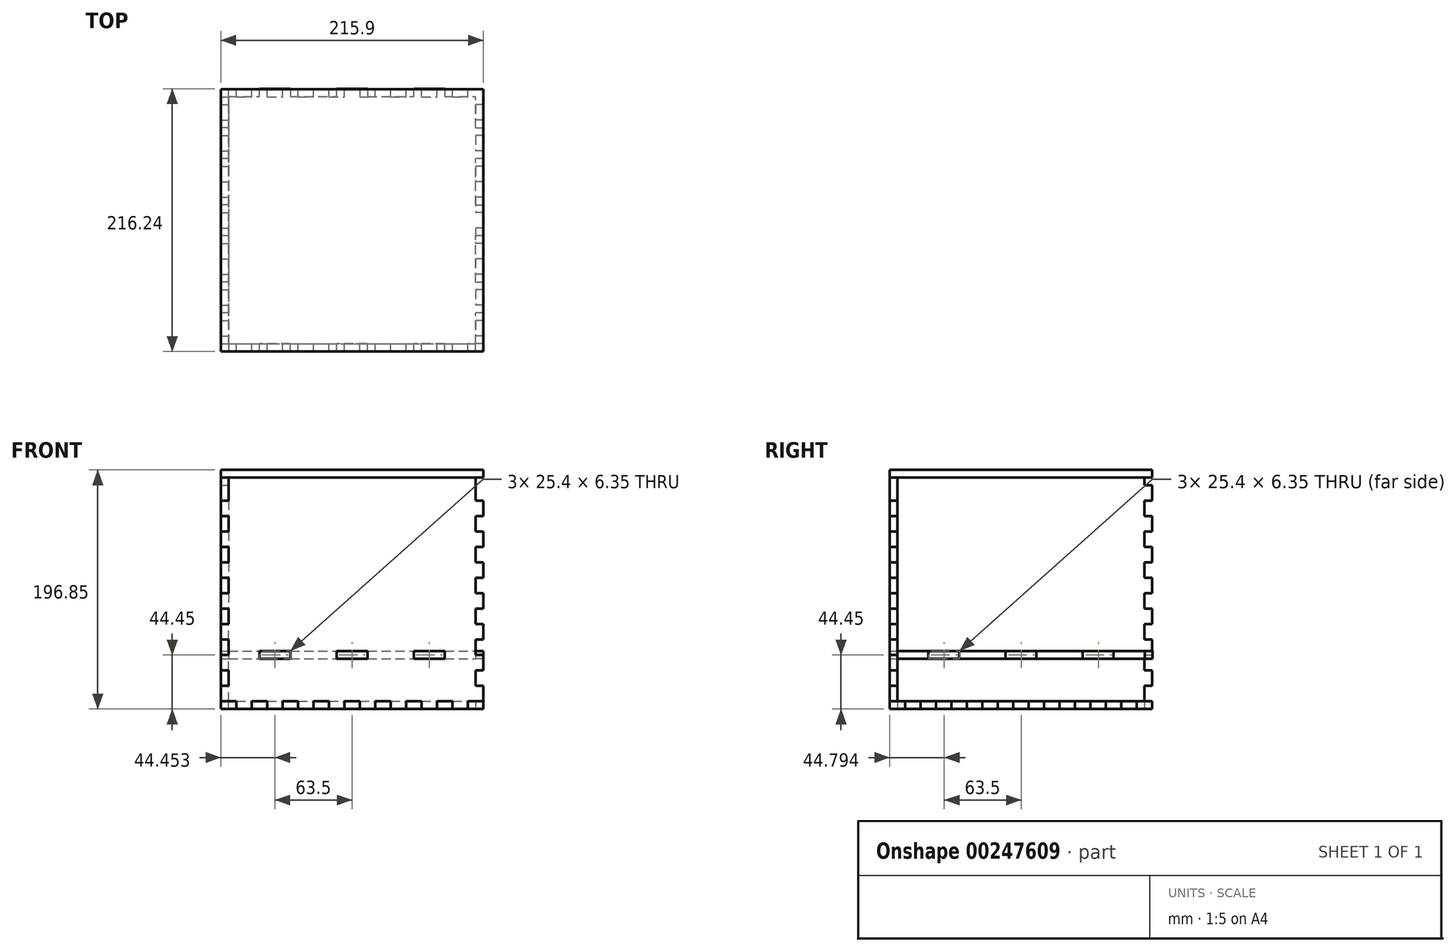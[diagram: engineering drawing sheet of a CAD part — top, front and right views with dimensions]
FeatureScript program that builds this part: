
annotation { "Feature Type Name" : "Feature", "Feature Type Description" : "" }
export const myFeature = defineFeature(function(context is Context, id is Id, definition is map)
    precondition{}
    {
        {
            var Q0;
            Q0=qCreatedBy(makeId("Top.planeOp"),FACE);
            var sketch = newSketch(context, id + "F0", { "sketchPlane" : qUnion([Q0])});
            skLineSegment(sketch, "E0.bottom", {"start": v(-61.86, 103.32) * mm, "end": v(-49.16, 103.32) * mm});
            skLineSegment(sketch, "E0.top", {"start": v(-61.86, -99.88) * mm, "end": v(-49.16, -99.88) * mm});
            skLineSegment(sketch, "E0.left", {"start": v(-68.2, 96.97) * mm, "end": v(-68.2, 84.27) * mm});
            skLineSegment(sketch, "E1.top", {"start": v(33.4, 109.67) * mm, "end": v(27.04, 109.67) * mm});
            skLineSegment(sketch, "E1.right", {"start": v(27.04, 103.32) * mm, "end": v(27.04, 109.67) * mm});
            skLineSegment(sketch, "E2.bottom", {"start": v(33.4, 109.67) * mm, "end": v(39.74, 109.67) * mm});
            skLineSegment(sketch, "E2.right", {"start": v(39.74, 109.67) * mm, "end": v(39.74, 103.32) * mm});
            skLineSegment(sketch, "E3.1.0.0", {"start": v(14.34, 103.32) * mm, "end": v(14.34, 109.67) * mm});
            skLineSegment(sketch, "E3.2.0.0", {"start": v(1.64, 103.32) * mm, "end": v(1.64, 109.67) * mm});
            skLineSegment(sketch, "E3.3.0.0", {"start": v(-11.06, 103.32) * mm, "end": v(-11.06, 109.67) * mm});
            skLineSegment(sketch, "E3.4.0.0", {"start": v(-23.76, 103.32) * mm, "end": v(-23.76, 109.67) * mm});
            skLineSegment(sketch, "E3.5.0.0", {"start": v(-36.46, 103.32) * mm, "end": v(-36.46, 109.67) * mm});
            skLineSegment(sketch, "E3.6.0.0", {"start": v(-49.16, 103.32) * mm, "end": v(-49.16, 109.67) * mm});
            skLineSegment(sketch, "E3.7.0.0", {"start": v(-61.86, 103.32) * mm, "end": v(-61.86, 109.67) * mm});
            skLineSegment(sketch, "E3.direction1", {"start": v(27.04, 103.32) * mm, "end": v(14.34, 103.32) * mm, "construction": true});
            skLineSegment(sketch, "E4", {"start": v(14.34, 109.67) * mm, "end": v(1.64, 109.67) * mm});
            skLineSegment(sketch, "E5", {"start": v(-23.76, 109.67) * mm, "end": v(-11.06, 109.67) * mm});
            skLineSegment(sketch, "E6", {"start": v(-36.46, 109.67) * mm, "end": v(-49.16, 109.67) * mm});
            skLineSegment(sketch, "E7", {"start": v(-68.2, 109.67) * mm, "end": v(-61.86, 109.67) * mm});
            skLineSegment(sketch, "E8.trimOffspring", {"start": v(-36.46, 103.32) * mm, "end": v(-23.76, 103.32) * mm});
            skLineSegment(sketch, "E9.trimOffspring", {"start": v(-11.06, 103.32) * mm, "end": v(1.64, 103.32) * mm});
            skLineSegment(sketch, "E10.trimOffspring", {"start": v(14.34, 103.32) * mm, "end": v(27.04, 103.32) * mm});
            skPoint(sketch, "E1.bottom.start.orphan", {"position": v(33.4, 103.32) * mm});
            skLineSegment(sketch, "E11.MirrorCS", {"start": v(135, 109.67) * mm, "end": v(128.64, 109.67) * mm});
            skLineSegment(sketch, "E12.MirrorCS", {"start": v(128.64, 103.32) * mm, "end": v(128.64, 109.67) * mm});
            skLineSegment(sketch, "E13.MirrorCS", {"start": v(103.24, 109.67) * mm, "end": v(115.94, 109.67) * mm});
            skLineSegment(sketch, "E14.MirrorCS", {"start": v(115.94, 103.32) * mm, "end": v(115.94, 109.67) * mm});
            skLineSegment(sketch, "E15.MirrorCS", {"start": v(103.24, 103.32) * mm, "end": v(103.24, 109.67) * mm});
            skLineSegment(sketch, "E16.MirrorCS", {"start": v(90.54, 103.32) * mm, "end": v(90.54, 109.67) * mm});
            skLineSegment(sketch, "E17.MirrorCS", {"start": v(90.54, 109.67) * mm, "end": v(77.84, 109.67) * mm});
            skLineSegment(sketch, "E18.MirrorCS", {"start": v(77.84, 103.32) * mm, "end": v(77.84, 109.67) * mm});
            skLineSegment(sketch, "E19.MirrorCS", {"start": v(65.14, 103.32) * mm, "end": v(65.14, 109.67) * mm});
            skLineSegment(sketch, "E20.MirrorCS", {"start": v(52.44, 109.67) * mm, "end": v(65.14, 109.67) * mm});
            skLineSegment(sketch, "E21.MirrorCS", {"start": v(52.44, 103.32) * mm, "end": v(52.44, 109.67) * mm});
            skLineSegment(sketch, "E22", {"start": v(39.74, 103.32) * mm, "end": v(52.44, 103.32) * mm});
            skLineSegment(sketch, "E23", {"start": v(65.14, 103.32) * mm, "end": v(77.84, 103.32) * mm});
            skLineSegment(sketch, "E24", {"start": v(90.54, 103.32) * mm, "end": v(103.24, 103.32) * mm});
            skLineSegment(sketch, "E25", {"start": v(115.94, 103.32) * mm, "end": v(128.64, 103.32) * mm});
            skLineSegment(sketch, "E26.MirrorCS", {"start": v(103.24, -106.23) * mm, "end": v(115.94, -106.23) * mm});
            skLineSegment(sketch, "E27.MirrorCS", {"start": v(27.04, -99.88) * mm, "end": v(27.04, -106.23) * mm});
            skLineSegment(sketch, "E28.MirrorCS", {"start": v(128.64, -99.88) * mm, "end": v(128.64, -106.23) * mm});
            skLineSegment(sketch, "E29.MirrorCS", {"start": v(33.4, -106.23) * mm, "end": v(39.74, -106.23) * mm});
            skLineSegment(sketch, "E30.MirrorCS", {"start": v(-49.16, -99.88) * mm, "end": v(-49.16, -106.23) * mm});
            skLineSegment(sketch, "E31.MirrorCS", {"start": v(-11.06, -99.88) * mm, "end": v(-11.06, -106.23) * mm});
            skLineSegment(sketch, "E32.MirrorCS", {"start": v(-61.86, -99.88) * mm, "end": v(-61.86, -106.23) * mm});
            skLineSegment(sketch, "E33.MirrorCS", {"start": v(39.74, -106.23) * mm, "end": v(39.74, -99.88) * mm});
            skLineSegment(sketch, "E34.MirrorCS", {"start": v(-68.2, -106.23) * mm, "end": v(-61.86, -106.23) * mm});
            skLineSegment(sketch, "E35.MirrorCS", {"start": v(90.54, -106.23) * mm, "end": v(77.84, -106.23) * mm});
            skLineSegment(sketch, "E36.MirrorCS", {"start": v(14.34, -106.23) * mm, "end": v(1.64, -106.23) * mm});
            skLineSegment(sketch, "E37.MirrorCS", {"start": v(-36.46, -99.88) * mm, "end": v(-36.46, -106.23) * mm});
            skLineSegment(sketch, "E38.MirrorCS", {"start": v(52.44, -99.88) * mm, "end": v(52.44, -106.23) * mm});
            skLineSegment(sketch, "E39.MirrorCS", {"start": v(135, -106.23) * mm, "end": v(128.64, -106.23) * mm});
            skLineSegment(sketch, "E40.MirrorCS", {"start": v(33.4, -106.23) * mm, "end": v(27.04, -106.23) * mm});
            skLineSegment(sketch, "E41.MirrorCS", {"start": v(77.84, -99.88) * mm, "end": v(77.84, -106.23) * mm});
            skLineSegment(sketch, "E42.MirrorCS", {"start": v(-36.46, -106.23) * mm, "end": v(-49.16, -106.23) * mm});
            skLineSegment(sketch, "E43.MirrorCS", {"start": v(103.24, -99.88) * mm, "end": v(103.24, -106.23) * mm});
            skLineSegment(sketch, "E44.MirrorCS", {"start": v(52.44, -106.23) * mm, "end": v(65.14, -106.23) * mm});
            skLineSegment(sketch, "E45.MirrorCS", {"start": v(-23.76, -106.23) * mm, "end": v(-11.06, -106.23) * mm});
            skLineSegment(sketch, "E46.MirrorCS", {"start": v(65.14, -99.88) * mm, "end": v(65.14, -106.23) * mm});
            skPoint(sketch, "E47.MirrorP", {"position": v(33.4, -99.88) * mm});
            skLineSegment(sketch, "E48.MirrorCS", {"start": v(14.34, -99.88) * mm, "end": v(14.34, -106.23) * mm});
            skLineSegment(sketch, "E49.MirrorCS", {"start": v(115.94, -99.88) * mm, "end": v(115.94, -106.23) * mm});
            skLineSegment(sketch, "E50.MirrorCS", {"start": v(90.54, -99.88) * mm, "end": v(90.54, -106.23) * mm});
            skLineSegment(sketch, "E51.MirrorCS", {"start": v(1.64, -99.88) * mm, "end": v(1.64, -106.23) * mm});
            skLineSegment(sketch, "E52.MirrorCS", {"start": v(-23.76, -99.88) * mm, "end": v(-23.76, -106.23) * mm});
            skLineSegment(sketch, "E53.trimOffspring", {"start": v(-36.46, -99.88) * mm, "end": v(-23.76, -99.88) * mm});
            skLineSegment(sketch, "E54.trimOffspring", {"start": v(-11.06, -99.88) * mm, "end": v(1.64, -99.88) * mm});
            skLineSegment(sketch, "E55.trimOffspring", {"start": v(14.34, -99.88) * mm, "end": v(27.04, -99.88) * mm});
            skLineSegment(sketch, "E56.trimOffspring", {"start": v(39.74, -99.88) * mm, "end": v(52.44, -99.88) * mm});
            skLineSegment(sketch, "E57.trimOffspring", {"start": v(65.14, -99.88) * mm, "end": v(77.84, -99.88) * mm});
            skLineSegment(sketch, "E58.trimOffspring", {"start": v(90.54, -99.88) * mm, "end": v(103.24, -99.88) * mm});
            skLineSegment(sketch, "E59.trimOffspring", {"start": v(115.94, -99.88) * mm, "end": v(128.64, -99.88) * mm});
            skPoint(sketch, "E60.start.orphan", {"position": v(-68.2, 1.72) * mm});
            skLineSegment(sketch, "E61.bottom", {"start": v(-74.56, 8.07) * mm, "end": v(-68.2, 8.07) * mm});
            skLineSegment(sketch, "E61.top", {"start": v(-74.56, -4.63) * mm, "end": v(-68.2, -4.63) * mm});
            skLineSegment(sketch, "E61.left", {"start": v(-74.56, 8.07) * mm, "end": v(-74.56, -4.63) * mm});
            skPoint(sketch, "E61.right.start.orphan", {"position": v(-61.86, 8.07) * mm});
            skPoint(sketch, "E62.orphan", {"position": v(-61.86, -4.63) * mm});
            skLineSegment(sketch, "E63.1.0.0", {"start": v(-74.56, 20.77) * mm, "end": v(-68.2, 20.77) * mm});
            skLineSegment(sketch, "E63.2.0.0", {"start": v(-74.56, 33.47) * mm, "end": v(-68.2, 33.47) * mm});
            skLineSegment(sketch, "E63.3.0.0", {"start": v(-74.56, 46.17) * mm, "end": v(-68.2, 46.17) * mm});
            skLineSegment(sketch, "E63.4.0.0", {"start": v(-74.56, 58.87) * mm, "end": v(-68.2, 58.87) * mm});
            skLineSegment(sketch, "E64", {"start": v(-74.56, 20.77) * mm, "end": v(-74.56, 33.47) * mm});
            skLineSegment(sketch, "E65", {"start": v(-74.56, 46.17) * mm, "end": v(-74.56, 58.87) * mm});
            skLineSegment(sketch, "E66.1.0.0", {"start": v(-74.56, -17.33) * mm, "end": v(-68.2, -17.33) * mm});
            skLineSegment(sketch, "E66.2.0.0", {"start": v(-74.56, -30.03) * mm, "end": v(-68.2, -30.03) * mm});
            skLineSegment(sketch, "E66.3.0.0", {"start": v(-74.56, -42.73) * mm, "end": v(-68.2, -42.73) * mm});
            skLineSegment(sketch, "E66.4.0.0", {"start": v(-74.56, -55.43) * mm, "end": v(-68.2, -55.43) * mm});
            skLineSegment(sketch, "E67", {"start": v(-74.56, -17.33) * mm, "end": v(-74.56, -30.03) * mm});
            skLineSegment(sketch, "E68", {"start": v(-74.56, -42.73) * mm, "end": v(-74.56, -55.43) * mm});
            skLineSegment(sketch, "E69.trimOffspring", {"start": v(-68.2, -55.43) * mm, "end": v(-68.2, -68.13) * mm});
            skLineSegment(sketch, "E70.trimOffspring", {"start": v(-68.2, -30.03) * mm, "end": v(-68.2, -42.73) * mm});
            skLineSegment(sketch, "E71.trimOffspring", {"start": v(-68.2, 20.77) * mm, "end": v(-68.2, 8.07) * mm});
            skLineSegment(sketch, "E72.trimOffspring", {"start": v(-68.2, 46.17) * mm, "end": v(-68.2, 33.47) * mm});
            skLineSegment(sketch, "E73.trimOffspring", {"start": v(-68.2, -4.63) * mm, "end": v(-68.2, -17.33) * mm});
            skLineSegment(sketch, "E74.1.0.0", {"start": v(-74.56, 71.57) * mm, "end": v(-68.2, 71.57) * mm});
            skLineSegment(sketch, "E74.2.0.0", {"start": v(-74.56, 84.27) * mm, "end": v(-68.2, 84.27) * mm});
            skLineSegment(sketch, "E75.0.3.0", {"start": v(-74.56, 96.97) * mm, "end": v(-68.2, 96.97) * mm});
            skLineSegment(sketch, "E76", {"start": v(-74.56, 71.57) * mm, "end": v(-74.56, 84.27) * mm});
            skLineSegment(sketch, "E77", {"start": v(-74.56, 96.97) * mm, "end": v(-74.56, 109.67) * mm});
            skLineSegment(sketch, "E78", {"start": v(-74.56, 109.67) * mm, "end": v(-68.2, 109.67) * mm});
            skPoint(sketch, "E79.orphan", {"position": v(-68.2, 103.32) * mm});
            skLineSegment(sketch, "E80.trimOffspring", {"start": v(-68.2, 71.57) * mm, "end": v(-68.2, 58.87) * mm});
            skLineSegment(sketch, "E81", {"start": v(135, 96.97) * mm, "end": v(135, 84.27) * mm});
            skLineSegment(sketch, "E82", {"start": v(33.4, 103.32) * mm, "end": v(33.4, -99.88) * mm});
            skLineSegment(sketch, "E83.MirrorCS", {"start": v(141.34, -55.43) * mm, "end": v(135, -55.43) * mm});
            skLineSegment(sketch, "E84.MirrorCS", {"start": v(141.34, -4.63) * mm, "end": v(135, -4.63) * mm});
            skLineSegment(sketch, "E85.MirrorCS", {"start": v(141.34, 33.47) * mm, "end": v(135, 33.47) * mm});
            skLineSegment(sketch, "E86.MirrorCS", {"start": v(141.34, 20.77) * mm, "end": v(135, 20.77) * mm});
            skLineSegment(sketch, "E87.MirrorCS", {"start": v(141.34, 8.07) * mm, "end": v(135, 8.07) * mm});
            skLineSegment(sketch, "E88.MirrorCS", {"start": v(141.34, 96.97) * mm, "end": v(141.34, 109.67) * mm});
            skLineSegment(sketch, "E89.MirrorCS", {"start": v(141.34, -17.33) * mm, "end": v(135, -17.33) * mm});
            skLineSegment(sketch, "E90.MirrorCS", {"start": v(141.34, -30.03) * mm, "end": v(135, -30.03) * mm});
            skLineSegment(sketch, "E91.MirrorCS", {"start": v(141.34, 71.57) * mm, "end": v(135, 71.57) * mm});
            skLineSegment(sketch, "E92.MirrorCS", {"start": v(141.34, -42.73) * mm, "end": v(135, -42.73) * mm});
            skLineSegment(sketch, "E93.MirrorCS", {"start": v(141.34, 58.87) * mm, "end": v(135, 58.87) * mm});
            skLineSegment(sketch, "E94.MirrorCS", {"start": v(141.34, 46.17) * mm, "end": v(135, 46.17) * mm});
            skLineSegment(sketch, "E95.MirrorCS", {"start": v(141.34, 96.97) * mm, "end": v(135, 96.97) * mm});
            skLineSegment(sketch, "E96.MirrorCS", {"start": v(141.34, 84.27) * mm, "end": v(135, 84.27) * mm});
            skPoint(sketch, "E97.MirrorP", {"position": v(135, 1.72) * mm});
            skLineSegment(sketch, "E98.MirrorCS", {"start": v(141.34, -17.33) * mm, "end": v(141.34, -30.03) * mm});
            skLineSegment(sketch, "E99.MirrorCS", {"start": v(141.34, 46.17) * mm, "end": v(141.34, 58.87) * mm});
            skLineSegment(sketch, "E100.MirrorCS", {"start": v(141.34, 8.07) * mm, "end": v(141.34, -4.63) * mm});
            skLineSegment(sketch, "E101.MirrorCS", {"start": v(141.34, 20.77) * mm, "end": v(141.34, 33.47) * mm});
            skLineSegment(sketch, "E102.MirrorCS", {"start": v(141.34, 71.57) * mm, "end": v(141.34, 84.27) * mm});
            skLineSegment(sketch, "E103.MirrorCS", {"start": v(141.34, -42.73) * mm, "end": v(141.34, -55.43) * mm});
            skPoint(sketch, "E104.MirrorP", {"position": v(135, 103.32) * mm});
            skLineSegment(sketch, "E105", {"start": v(135, 109.67) * mm, "end": v(141.34, 109.67) * mm});
            skLineSegment(sketch, "E106.trimOffspring", {"start": v(135, 71.57) * mm, "end": v(135, 58.87) * mm});
            skLineSegment(sketch, "E107.trimOffspring", {"start": v(135, 46.17) * mm, "end": v(135, 33.47) * mm});
            skLineSegment(sketch, "E108.trimOffspring", {"start": v(135, 20.77) * mm, "end": v(135, 8.07) * mm});
            skLineSegment(sketch, "E109.trimOffspring", {"start": v(135, -4.63) * mm, "end": v(135, -17.33) * mm});
            skLineSegment(sketch, "E110.trimOffspring", {"start": v(135, -30.03) * mm, "end": v(135, -42.73) * mm});
            skLineSegment(sketch, "E111.trimOffspring", {"start": v(135, -55.43) * mm, "end": v(135, -68.13) * mm});
            skLineSegment(sketch, "E112.1.0.0", {"start": v(-74.56, -68.13) * mm, "end": v(-68.2, -68.13) * mm});
            skLineSegment(sketch, "E112.2.0.0", {"start": v(-74.56, -80.83) * mm, "end": v(-68.2, -80.83) * mm});
            skLineSegment(sketch, "E112.3.0.0", {"start": v(-74.56, -93.53) * mm, "end": v(-68.2, -93.53) * mm});
            skLineSegment(sketch, "E113", {"start": v(-74.56, -68.13) * mm, "end": v(-74.56, -80.83) * mm});
            skLineSegment(sketch, "E114", {"start": v(-74.56, -93.53) * mm, "end": v(-74.56, -106.23) * mm});
            skLineSegment(sketch, "E115", {"start": v(-74.56, -106.23) * mm, "end": v(-68.2, -106.23) * mm});
            skLineSegment(sketch, "E116.trimOffspring", {"start": v(-68.2, -80.83) * mm, "end": v(-68.2, -93.53) * mm});
            skPoint(sketch, "E117.orphan", {"position": v(-68.2, -99.88) * mm});
            skLineSegment(sketch, "E118.MirrorCS", {"start": v(141.34, -93.53) * mm, "end": v(141.34, -106.23) * mm});
            skLineSegment(sketch, "E119.MirrorCS", {"start": v(141.34, -80.83) * mm, "end": v(135, -80.83) * mm});
            skLineSegment(sketch, "E120.MirrorCS", {"start": v(141.34, -68.13) * mm, "end": v(135, -68.13) * mm});
            skLineSegment(sketch, "E121.MirrorCS", {"start": v(141.34, -68.13) * mm, "end": v(141.34, -80.83) * mm});
            skLineSegment(sketch, "E122.MirrorCS", {"start": v(141.34, -93.53) * mm, "end": v(135, -93.53) * mm});
            skLineSegment(sketch, "E123.MirrorCS", {"start": v(141.34, -106.23) * mm, "end": v(135, -106.23) * mm});
            skLineSegment(sketch, "E124.trimOffspring", {"start": v(135, -80.83) * mm, "end": v(135, -93.53) * mm});
            skPoint(sketch, "E125.MirrorCS.end.orphan", {"position": v(135, -106.23) * mm});
            skSolve(sketch);
        }
        {
            var Q0;
            Q0 = qSketchRegion(id + "F0", true);
            extrude(context, id + "F1", {"entities" : qUnion([Q0]), "depth" : 6.35 * mm, "offsetDistance" : 25.4 * mm});
        }
        {
            var Q0;
            Q0=makeQuery(id+"F1.opExtrude","SWEPT_FACE",FACE,{"disambiguationData":[OSD([sQuery(id+"F0.wireOp",EDGE,"E55.trimOffspring")])]});
            var sketch = newSketch(context, id + "F2", { "sketchPlane" : qUnion([Q0])});
            skLineSegment(sketch, "E126.0.0", {"start": v(14.34, 0) * mm, "end": v(27.04, 0) * mm});
            skLineSegment(sketch, "E126.0.1", {"start": v(27.04, 0) * mm, "end": v(27.04, 6.35) * mm});
            skLineSegment(sketch, "E126.0.3", {"start": v(14.34, 6.35) * mm, "end": v(14.34, 0) * mm});
            skLineSegment(sketch, "E127.0.0", {"start": v(-11.06, 0) * mm, "end": v(1.64, 0) * mm});
            skLineSegment(sketch, "E127.0.1", {"start": v(1.64, 0) * mm, "end": v(1.64, 6.35) * mm});
            skLineSegment(sketch, "E127.0.3", {"start": v(-11.06, 6.35) * mm, "end": v(-11.06, 0) * mm});
            skLineSegment(sketch, "E128.0.0", {"start": v(-36.46, 0) * mm, "end": v(-23.76, 0) * mm});
            skLineSegment(sketch, "E128.0.1", {"start": v(-23.76, 0) * mm, "end": v(-23.76, 6.35) * mm});
            skLineSegment(sketch, "E128.0.3", {"start": v(-36.46, 6.35) * mm, "end": v(-36.46, 0) * mm});
            skLineSegment(sketch, "E129.0.0", {"start": v(-61.86, 0) * mm, "end": v(-49.16, 0) * mm});
            skLineSegment(sketch, "E129.0.1", {"start": v(-49.16, 0) * mm, "end": v(-49.16, 6.35) * mm});
            skLineSegment(sketch, "E129.0.3", {"start": v(-61.86, 6.35) * mm, "end": v(-61.86, 0) * mm});
            skPoint(sketch, "E130.0", {"position": v(46.1, 6.35) * mm});
            skLineSegment(sketch, "E131.0.0", {"start": v(39.74, 0) * mm, "end": v(52.44, 0) * mm});
            skLineSegment(sketch, "E131.0.1", {"start": v(52.44, 0) * mm, "end": v(52.44, 6.35) * mm});
            skLineSegment(sketch, "E131.0.3", {"start": v(39.74, 6.35) * mm, "end": v(39.74, 0) * mm});
            skLineSegment(sketch, "E131.1.0", {"start": v(65.14, 0) * mm, "end": v(77.84, 0) * mm});
            skLineSegment(sketch, "E131.1.1", {"start": v(77.84, 0) * mm, "end": v(77.84, 6.35) * mm});
            skLineSegment(sketch, "E131.1.3", {"start": v(65.14, 6.35) * mm, "end": v(65.14, 0) * mm});
            skLineSegment(sketch, "E131.2.0", {"start": v(90.54, 0) * mm, "end": v(103.24, 0) * mm});
            skLineSegment(sketch, "E131.2.1", {"start": v(103.24, 0) * mm, "end": v(103.24, 6.35) * mm});
            skLineSegment(sketch, "E131.2.3", {"start": v(90.54, 6.35) * mm, "end": v(90.54, 0) * mm});
            skLineSegment(sketch, "E131.3.0", {"start": v(115.94, 0) * mm, "end": v(128.64, 0) * mm});
            skLineSegment(sketch, "E131.3.1", {"start": v(128.64, 0) * mm, "end": v(128.64, 6.35) * mm});
            skLineSegment(sketch, "E131.3.3", {"start": v(115.94, 6.35) * mm, "end": v(115.94, 0) * mm});
            skLineSegment(sketch, "E132", {"start": v(-49.16, 6.35) * mm, "end": v(-36.46, 6.35) * mm});
            skLineSegment(sketch, "E133", {"start": v(-23.76, 6.35) * mm, "end": v(-11.06, 6.35) * mm});
            skLineSegment(sketch, "E134", {"start": v(1.64, 6.35) * mm, "end": v(14.34, 6.35) * mm});
            skLineSegment(sketch, "E135", {"start": v(27.04, 6.35) * mm, "end": v(39.74, 6.35) * mm});
            skLineSegment(sketch, "E136", {"start": v(52.44, 6.35) * mm, "end": v(65.14, 6.35) * mm});
            skLineSegment(sketch, "E137", {"start": v(77.84, 6.35) * mm, "end": v(90.54, 6.35) * mm});
            skLineSegment(sketch, "E138", {"start": v(103.24, 6.35) * mm, "end": v(115.94, 6.35) * mm});
            skPoint(sketch, "E139.end.orphan", {"position": v(33.4, 6.35) * mm});
            skLineSegment(sketch, "E140", {"start": v(-68.2, 184.15) * mm, "end": v(-68.2, 171.45) * mm});
            skLineSegment(sketch, "E141.MirrorCS", {"start": v(-74.56, 19.05) * mm, "end": v(-68.2, 19.05) * mm});
            skLineSegment(sketch, "E142.MirrorCS", {"start": v(-74.56, 31.75) * mm, "end": v(-68.2, 31.75) * mm});
            skLineSegment(sketch, "E143.MirrorCS", {"start": v(-74.56, 107.95) * mm, "end": v(-68.2, 107.95) * mm});
            skLineSegment(sketch, "E144.MirrorCS", {"start": v(-74.56, 57.15) * mm, "end": v(-68.2, 57.15) * mm});
            skLineSegment(sketch, "E145.MirrorCS", {"start": v(-74.56, 171.45) * mm, "end": v(-68.2, 171.45) * mm});
            skLineSegment(sketch, "E146.MirrorCS", {"start": v(-74.56, 44.45) * mm, "end": v(-68.2, 44.45) * mm});
            skLineSegment(sketch, "E147.MirrorCS", {"start": v(-74.56, 158.75) * mm, "end": v(-68.2, 158.75) * mm});
            skLineSegment(sketch, "E148.MirrorCS", {"start": v(-74.56, 82.55) * mm, "end": v(-68.2, 82.55) * mm});
            skLineSegment(sketch, "E149.MirrorCS", {"start": v(-74.56, 69.85) * mm, "end": v(-68.2, 69.85) * mm});
            skLineSegment(sketch, "E150.MirrorCS", {"start": v(-74.56, 120.65) * mm, "end": v(-68.2, 120.65) * mm});
            skLineSegment(sketch, "E151.MirrorCS", {"start": v(-74.56, 6.35) * mm, "end": v(-68.2, 6.35) * mm});
            skLineSegment(sketch, "E152.MirrorCS", {"start": v(-74.56, 133.35) * mm, "end": v(-68.2, 133.35) * mm});
            skLineSegment(sketch, "E153.MirrorCS", {"start": v(-74.56, 95.25) * mm, "end": v(-68.2, 95.25) * mm});
            skLineSegment(sketch, "E154.MirrorCS", {"start": v(-74.56, 146.05) * mm, "end": v(-68.2, 146.05) * mm});
            skLineSegment(sketch, "E155.MirrorCS", {"start": v(-74.56, 171.45) * mm, "end": v(-74.56, 158.75) * mm});
            skLineSegment(sketch, "E156.MirrorCS", {"start": v(-74.56, 69.85) * mm, "end": v(-74.56, 57.15) * mm});
            skPoint(sketch, "E157.MirrorP", {"position": v(-68.2, 88.9) * mm});
            skLineSegment(sketch, "E158.MirrorCS", {"start": v(-74.56, 95.25) * mm, "end": v(-74.56, 82.55) * mm});
            skLineSegment(sketch, "E159.MirrorCS", {"start": v(-61.86, 6.35) * mm, "end": v(-61.86, 6.35) * mm});
            skLineSegment(sketch, "E160.MirrorCS", {"start": v(-74.56, 6.35) * mm, "end": v(-74.56, 19.05) * mm});
            skLineSegment(sketch, "E161.MirrorCS", {"start": v(-74.56, 31.75) * mm, "end": v(-74.56, 44.45) * mm});
            skLineSegment(sketch, "E162.MirrorCS", {"start": v(-74.56, 146.05) * mm, "end": v(-74.56, 133.35) * mm});
            skLineSegment(sketch, "E163.MirrorCS", {"start": v(-74.56, 120.65) * mm, "end": v(-74.56, 107.95) * mm});
            skLineSegment(sketch, "E164.trimOffspring", {"start": v(-68.2, 158.75) * mm, "end": v(-68.2, 146.05) * mm});
            skLineSegment(sketch, "E165.trimOffspring", {"start": v(-68.2, 133.35) * mm, "end": v(-68.2, 120.65) * mm});
            skLineSegment(sketch, "E166.trimOffspring", {"start": v(-68.2, 107.95) * mm, "end": v(-68.2, 95.25) * mm});
            skLineSegment(sketch, "E167.trimOffspring", {"start": v(-68.2, 82.55) * mm, "end": v(-68.2, 69.85) * mm});
            skLineSegment(sketch, "E168.trimOffspring", {"start": v(-68.2, 57.15) * mm, "end": v(-68.2, 44.45) * mm});
            skLineSegment(sketch, "E169.trimOffspring", {"start": v(-68.2, 31.75) * mm, "end": v(-68.2, 19.05) * mm});
            skLineSegment(sketch, "E170.trimOffspring", {"start": v(-68.2, 6.35) * mm, "end": v(-61.86, 6.35) * mm});
            skPoint(sketch, "E171.0.end.orphan", {"position": v(-68.2, 6.35) * mm});
            skLineSegment(sketch, "E172.MirrorCS", {"start": v(141.34, 31.75) * mm, "end": v(135, 31.75) * mm});
            skLineSegment(sketch, "E173.MirrorCS", {"start": v(141.34, 6.35) * mm, "end": v(135, 6.35) * mm});
            skLineSegment(sketch, "E174.MirrorCS", {"start": v(141.34, 107.95) * mm, "end": v(135, 107.95) * mm});
            skLineSegment(sketch, "E175.MirrorCS", {"start": v(141.34, 19.05) * mm, "end": v(135, 19.05) * mm});
            skLineSegment(sketch, "E176.MirrorCS", {"start": v(141.34, 120.65) * mm, "end": v(135, 120.65) * mm});
            skLineSegment(sketch, "E177.MirrorCS", {"start": v(141.34, 146.05) * mm, "end": v(135, 146.05) * mm});
            skLineSegment(sketch, "E178.MirrorCS", {"start": v(141.34, 133.35) * mm, "end": v(135, 133.35) * mm});
            skLineSegment(sketch, "E179.MirrorCS", {"start": v(141.34, 158.75) * mm, "end": v(135, 158.75) * mm});
            skLineSegment(sketch, "E180.MirrorCS", {"start": v(141.34, 95.25) * mm, "end": v(135, 95.25) * mm});
            skLineSegment(sketch, "E181.MirrorCS", {"start": v(141.34, 82.55) * mm, "end": v(135, 82.55) * mm});
            skLineSegment(sketch, "E182.MirrorCS", {"start": v(141.34, 69.85) * mm, "end": v(135, 69.85) * mm});
            skLineSegment(sketch, "E183.MirrorCS", {"start": v(141.34, 171.45) * mm, "end": v(135, 171.45) * mm});
            skLineSegment(sketch, "E184.MirrorCS", {"start": v(141.34, 44.45) * mm, "end": v(135, 44.45) * mm});
            skLineSegment(sketch, "E185.MirrorCS", {"start": v(141.34, 57.15) * mm, "end": v(135, 57.15) * mm});
            skLineSegment(sketch, "E186.MirrorCS", {"start": v(141.34, 171.45) * mm, "end": v(141.34, 158.75) * mm});
            skLineSegment(sketch, "E187.MirrorCS", {"start": v(141.34, 146.05) * mm, "end": v(141.34, 133.35) * mm});
            skLineSegment(sketch, "E188.MirrorCS", {"start": v(141.34, 95.25) * mm, "end": v(141.34, 82.55) * mm});
            skPoint(sketch, "E189.MirrorP", {"position": v(135, 6.35) * mm});
            skLineSegment(sketch, "E190.MirrorCS", {"start": v(141.34, 6.35) * mm, "end": v(141.34, 19.05) * mm});
            skLineSegment(sketch, "E191.MirrorCS", {"start": v(141.34, 120.65) * mm, "end": v(141.34, 107.95) * mm});
            skLineSegment(sketch, "E192.MirrorCS", {"start": v(141.34, 69.85) * mm, "end": v(141.34, 57.15) * mm});
            skLineSegment(sketch, "E193.MirrorCS", {"start": v(141.34, 31.75) * mm, "end": v(141.34, 44.45) * mm});
            skPoint(sketch, "E194.MirrorP", {"position": v(135, 88.9) * mm});
            skLineSegment(sketch, "E195", {"start": v(135, 6.35) * mm, "end": v(128.64, 6.35) * mm});
            skLineSegment(sketch, "E196", {"start": v(135, 19.05) * mm, "end": v(135, 31.75) * mm});
            skLineSegment(sketch, "E197", {"start": v(135, 44.45) * mm, "end": v(135, 57.15) * mm});
            skLineSegment(sketch, "E198", {"start": v(135, 69.85) * mm, "end": v(135, 82.55) * mm});
            skLineSegment(sketch, "E199", {"start": v(135, 95.25) * mm, "end": v(135, 107.95) * mm});
            skLineSegment(sketch, "E200", {"start": v(135, 120.65) * mm, "end": v(135, 133.35) * mm});
            skLineSegment(sketch, "E201", {"start": v(135, 146.05) * mm, "end": v(135, 158.75) * mm});
            skLineSegment(sketch, "E202", {"start": v(135, 184.15) * mm, "end": v(135, 171.45) * mm});
            skLineSegment(sketch, "E203", {"start": v(-68.2, 184.15) * mm, "end": v(-68.2, 190.5) * mm});
            skLineSegment(sketch, "E204", {"start": v(-68.2, 190.5) * mm, "end": v(115.94, 190.5) * mm});
            skLineSegment(sketch, "E205", {"start": v(135, 190.5) * mm, "end": v(135, 184.15) * mm});
            skLineSegment(sketch, "E206.trimOffspring", {"start": v(128.64, 190.5) * mm, "end": v(135, 190.5) * mm});
            skLineSegment(sketch, "E207", {"start": v(128.64, 190.5) * mm, "end": v(115.94, 190.5) * mm});
            skSolve(sketch);
        }
        {
            var Q0;
            Q0 = qSketchRegion(id + "F2", true);
            extrude(context, id + "F3", {"entities" : qUnion([Q0]), "depth" : 6.35 * mm, "offsetDistance" : 25.4 * mm});
        }
        {
            var Q0;
            Q0=makeQuery(id+"F1.opExtrude","SWEPT_FACE",FACE,{"disambiguationData":[OSD([sQuery(id+"F0.wireOp",EDGE,"E71.trimOffspring")])]});
            var sketch = newSketch(context, id + "F4", { "sketchPlane" : qUnion([Q0])});
            skLineSegment(sketch, "E208.0.0", {"start": v(-96.97, 0) * mm, "end": v(-84.27, 0) * mm});
            skLineSegment(sketch, "E208.0.1", {"start": v(-84.27, 0) * mm, "end": v(-84.27, 6.35) * mm});
            skLineSegment(sketch, "E208.0.3", {"start": v(-96.97, 6.35) * mm, "end": v(-96.97, 0) * mm});
            skLineSegment(sketch, "E209.0.0", {"start": v(-71.57, 0) * mm, "end": v(-58.87, 0) * mm});
            skLineSegment(sketch, "E209.0.1", {"start": v(-58.87, 0) * mm, "end": v(-58.87, 6.35) * mm});
            skLineSegment(sketch, "E209.0.3", {"start": v(-71.57, 6.35) * mm, "end": v(-71.57, 0) * mm});
            skLineSegment(sketch, "E210.0.0", {"start": v(-46.17, 0) * mm, "end": v(-33.47, 0) * mm});
            skLineSegment(sketch, "E210.0.1", {"start": v(-33.47, 0) * mm, "end": v(-33.47, 6.35) * mm});
            skLineSegment(sketch, "E210.0.3", {"start": v(-46.17, 6.35) * mm, "end": v(-46.17, 0) * mm});
            skLineSegment(sketch, "E211.0.0", {"start": v(-20.77, 0) * mm, "end": v(-8.07, 0) * mm});
            skLineSegment(sketch, "E211.0.1", {"start": v(-8.07, 0) * mm, "end": v(-8.07, 6.35) * mm});
            skLineSegment(sketch, "E211.0.3", {"start": v(-20.77, 6.35) * mm, "end": v(-20.77, 0) * mm});
            skLineSegment(sketch, "E212.0.0", {"start": v(4.63, 0) * mm, "end": v(17.33, 0) * mm});
            skLineSegment(sketch, "E212.0.1", {"start": v(17.33, 0) * mm, "end": v(17.33, 6.35) * mm});
            skLineSegment(sketch, "E212.0.3", {"start": v(4.63, 6.35) * mm, "end": v(4.63, 0) * mm});
            skLineSegment(sketch, "E213.0.0", {"start": v(30.03, 0) * mm, "end": v(42.73, 0) * mm});
            skLineSegment(sketch, "E213.0.1", {"start": v(42.73, 0) * mm, "end": v(42.73, 6.35) * mm});
            skLineSegment(sketch, "E213.0.3", {"start": v(30.03, 6.35) * mm, "end": v(30.03, 0) * mm});
            skLineSegment(sketch, "E214.0.0", {"start": v(55.43, 0) * mm, "end": v(68.13, 0) * mm});
            skLineSegment(sketch, "E214.0.1", {"start": v(68.13, 0) * mm, "end": v(68.13, 6.35) * mm});
            skLineSegment(sketch, "E214.0.3", {"start": v(55.43, 6.35) * mm, "end": v(55.43, 0) * mm});
            skLineSegment(sketch, "E215.0.0", {"start": v(80.83, 0) * mm, "end": v(93.53, 0) * mm});
            skLineSegment(sketch, "E215.0.1", {"start": v(93.53, 0) * mm, "end": v(93.53, 6.35) * mm});
            skLineSegment(sketch, "E215.0.3", {"start": v(80.83, 6.35) * mm, "end": v(80.83, 0) * mm});
            skLineSegment(sketch, "E216.0.1", {"start": v(99.88, 19.05) * mm, "end": v(106.23, 19.05) * mm});
            skLineSegment(sketch, "E216.0.2", {"start": v(106.23, 19.05) * mm, "end": v(106.23, 31.75) * mm});
            skLineSegment(sketch, "E216.0.3", {"start": v(106.23, 31.75) * mm, "end": v(99.88, 31.75) * mm});
            skLineSegment(sketch, "E217.0.1", {"start": v(99.88, 44.45) * mm, "end": v(106.23, 44.45) * mm});
            skLineSegment(sketch, "E217.0.2", {"start": v(106.23, 44.45) * mm, "end": v(106.23, 57.15) * mm});
            skLineSegment(sketch, "E217.0.3", {"start": v(106.23, 57.15) * mm, "end": v(99.88, 57.15) * mm});
            skLineSegment(sketch, "E218.0.1", {"start": v(99.88, 69.85) * mm, "end": v(106.23, 69.85) * mm});
            skLineSegment(sketch, "E218.0.2", {"start": v(106.23, 69.85) * mm, "end": v(106.23, 82.55) * mm});
            skLineSegment(sketch, "E218.0.3", {"start": v(106.23, 82.55) * mm, "end": v(99.88, 82.55) * mm});
            skLineSegment(sketch, "E219.0.1", {"start": v(99.88, 95.25) * mm, "end": v(106.23, 95.25) * mm});
            skLineSegment(sketch, "E219.0.2", {"start": v(106.23, 95.25) * mm, "end": v(106.23, 107.95) * mm});
            skLineSegment(sketch, "E219.0.3", {"start": v(106.23, 107.95) * mm, "end": v(99.88, 107.95) * mm});
            skLineSegment(sketch, "E220.0.1", {"start": v(99.88, 120.65) * mm, "end": v(106.23, 120.65) * mm});
            skLineSegment(sketch, "E220.0.2", {"start": v(106.23, 120.65) * mm, "end": v(106.23, 133.35) * mm});
            skLineSegment(sketch, "E220.0.3", {"start": v(106.23, 133.35) * mm, "end": v(99.88, 133.35) * mm});
            skLineSegment(sketch, "E221.0.1", {"start": v(99.88, 146.05) * mm, "end": v(106.23, 146.05) * mm});
            skLineSegment(sketch, "E221.0.2", {"start": v(106.23, 146.05) * mm, "end": v(106.23, 158.75) * mm});
            skLineSegment(sketch, "E221.0.3", {"start": v(106.23, 158.75) * mm, "end": v(99.88, 158.75) * mm});
            skLineSegment(sketch, "E222.0.1", {"start": v(99.88, 171.45) * mm, "end": v(106.23, 171.45) * mm});
            skLineSegment(sketch, "E222.0.2", {"start": v(106.23, 171.45) * mm, "end": v(106.23, 171.45) * mm});
            skLineSegment(sketch, "E222.0.3", {"start": v(99.88, 171.45) * mm, "end": v(106.23, 171.45) * mm});
            skLineSegment(sketch, "E223", {"start": v(-84.27, 6.35) * mm, "end": v(-71.57, 6.35) * mm});
            skLineSegment(sketch, "E224", {"start": v(-58.87, 6.35) * mm, "end": v(-46.17, 6.35) * mm});
            skLineSegment(sketch, "E225", {"start": v(-33.47, 6.35) * mm, "end": v(-20.77, 6.35) * mm});
            skLineSegment(sketch, "E226", {"start": v(-8.07, 6.35) * mm, "end": v(4.63, 6.35) * mm});
            skLineSegment(sketch, "E227", {"start": v(17.33, 6.35) * mm, "end": v(30.03, 6.35) * mm});
            skLineSegment(sketch, "E228", {"start": v(42.73, 6.35) * mm, "end": v(55.43, 6.35) * mm});
            skLineSegment(sketch, "E229", {"start": v(68.13, 6.35) * mm, "end": v(80.83, 6.35) * mm});
            skLineSegment(sketch, "E230", {"start": v(93.53, 6.35) * mm, "end": v(99.88, 6.35) * mm});
            skLineSegment(sketch, "E231", {"start": v(99.88, 6.35) * mm, "end": v(99.88, 19.05) * mm});
            skLineSegment(sketch, "E232", {"start": v(99.88, 31.75) * mm, "end": v(99.88, 44.45) * mm});
            skLineSegment(sketch, "E233", {"start": v(99.88, 57.15) * mm, "end": v(99.88, 69.85) * mm});
            skLineSegment(sketch, "E234", {"start": v(99.88, 95.25) * mm, "end": v(99.88, 82.55) * mm});
            skLineSegment(sketch, "E235", {"start": v(99.88, 120.65) * mm, "end": v(99.88, 107.95) * mm});
            skLineSegment(sketch, "E236", {"start": v(99.88, 146.05) * mm, "end": v(99.88, 133.35) * mm});
            skLineSegment(sketch, "E237", {"start": v(99.88, 171.45) * mm, "end": v(99.88, 158.75) * mm});
            skPoint(sketch, "E238.0.end.orphan", {"position": v(-109.67, 6.35) * mm});
            skPoint(sketch, "E238.0.start.orphan", {"position": v(-96.97, 6.35) * mm});
            skPoint(sketch, "E239.0", {"position": v(-103.32, 6.35) * mm});
            skLineSegment(sketch, "E240.MirrorCS", {"start": v(-109.67, 133.35) * mm, "end": v(-103.32, 133.35) * mm});
            skLineSegment(sketch, "E241.MirrorCS", {"start": v(-103.32, 44.45) * mm, "end": v(-109.67, 44.45) * mm});
            skLineSegment(sketch, "E242.MirrorCS", {"start": v(-109.67, 107.95) * mm, "end": v(-103.32, 107.95) * mm});
            skLineSegment(sketch, "E243.MirrorCS", {"start": v(-103.32, 171.45) * mm, "end": v(-109.67, 171.45) * mm});
            skLineSegment(sketch, "E244.MirrorCS", {"start": v(-96.97, 6.35) * mm, "end": v(-103.32, 6.35) * mm});
            skLineSegment(sketch, "E245.MirrorCS", {"start": v(-103.32, 95.25) * mm, "end": v(-109.67, 95.25) * mm});
            skLineSegment(sketch, "E246.MirrorCS", {"start": v(-103.32, 146.05) * mm, "end": v(-109.67, 146.05) * mm});
            skLineSegment(sketch, "E247.MirrorCS", {"start": v(-109.67, 158.75) * mm, "end": v(-103.32, 158.75) * mm});
            skLineSegment(sketch, "E248.MirrorCS", {"start": v(-103.32, 19.05) * mm, "end": v(-109.67, 19.05) * mm});
            skLineSegment(sketch, "E249.MirrorCS", {"start": v(-109.67, 82.55) * mm, "end": v(-103.32, 82.55) * mm});
            skLineSegment(sketch, "E250.MirrorCS", {"start": v(-103.32, 69.85) * mm, "end": v(-109.67, 69.85) * mm});
            skLineSegment(sketch, "E251.MirrorCS", {"start": v(-109.67, 31.75) * mm, "end": v(-103.32, 31.75) * mm});
            skLineSegment(sketch, "E252.MirrorCS", {"start": v(-103.32, 120.65) * mm, "end": v(-109.67, 120.65) * mm});
            skLineSegment(sketch, "E253.MirrorCS", {"start": v(-109.67, 57.15) * mm, "end": v(-103.32, 57.15) * mm});
            skLineSegment(sketch, "E254.MirrorCS", {"start": v(-109.67, 184.15) * mm, "end": v(-103.32, 184.15) * mm});
            skLineSegment(sketch, "E255.MirrorCS", {"start": v(-109.67, 146.05) * mm, "end": v(-109.67, 158.75) * mm});
            skLineSegment(sketch, "E256.MirrorCS", {"start": v(-103.32, 120.65) * mm, "end": v(-103.32, 107.95) * mm});
            skLineSegment(sketch, "E257.MirrorCS", {"start": v(-103.32, 31.75) * mm, "end": v(-103.32, 44.45) * mm});
            skLineSegment(sketch, "E258.MirrorCS", {"start": v(-103.32, 171.45) * mm, "end": v(-103.32, 158.75) * mm});
            skLineSegment(sketch, "E259.MirrorCS", {"start": v(-109.67, 44.45) * mm, "end": v(-109.67, 57.15) * mm});
            skLineSegment(sketch, "E260.MirrorCS", {"start": v(-109.67, 69.85) * mm, "end": v(-109.67, 82.55) * mm});
            skLineSegment(sketch, "E261.MirrorCS", {"start": v(-103.32, 146.05) * mm, "end": v(-103.32, 133.35) * mm});
            skLineSegment(sketch, "E262.MirrorCS", {"start": v(-103.32, 57.15) * mm, "end": v(-103.32, 69.85) * mm});
            skLineSegment(sketch, "E263.MirrorCS", {"start": v(-109.67, 120.65) * mm, "end": v(-109.67, 133.35) * mm});
            skLineSegment(sketch, "E264.MirrorCS", {"start": v(-103.32, 95.25) * mm, "end": v(-103.32, 82.55) * mm});
            skLineSegment(sketch, "E265.MirrorCS", {"start": v(-109.67, 19.05) * mm, "end": v(-109.67, 31.75) * mm});
            skLineSegment(sketch, "E266.MirrorCS", {"start": v(-109.67, 171.45) * mm, "end": v(-109.67, 184.15) * mm});
            skLineSegment(sketch, "E267.MirrorCS", {"start": v(-103.32, 6.35) * mm, "end": v(-103.32, 19.05) * mm});
            skLineSegment(sketch, "E268.MirrorCS", {"start": v(-109.67, 95.25) * mm, "end": v(-109.67, 107.95) * mm});
            skPoint(sketch, "E269.start.orphan", {"position": v(-1.72, 6.35) * mm});
            skLineSegment(sketch, "E270.MirrorCS", {"start": v(-103.32, 184.15) * mm, "end": v(-103.32, 184.15) * mm});
            skLineSegment(sketch, "E271.MirrorCS", {"start": v(99.88, 171.45) * mm, "end": v(99.88, 171.45) * mm});
            skPoint(sketch, "E272.MirrorP", {"position": v(-109.67, 196.85) * mm});
            skPoint(sketch, "E273.MirrorP", {"position": v(-103.32, 196.85) * mm});
            skPoint(sketch, "E274.end.orphan", {"position": v(106.23, 101.6) * mm});
            skPoint(sketch, "E274.start.orphan", {"position": v(-109.67, 101.6) * mm});
            skLineSegment(sketch, "E275", {"start": v(-103.32, 190.5) * mm, "end": v(-103.32, 184.15) * mm});
            skLineSegment(sketch, "E276", {"start": v(-103.32, 190.5) * mm, "end": v(99.88, 190.5) * mm});
            skLineSegment(sketch, "E277", {"start": v(99.88, 190.5) * mm, "end": v(106.23, 190.5) * mm});
            skLineSegment(sketch, "E278", {"start": v(106.23, 190.5) * mm, "end": v(106.23, 171.45) * mm});
            skSolve(sketch);
        }
        {
            var Q0;
            Q0 = qSketchRegion(id + "F4", true);
            extrude(context, id + "F5", {"entities" : qUnion([Q0]), "depth" : 6.35 * mm, "offsetDistance" : 25.4 * mm});
        }
        {
            var Q0;
            Q0=makeQuery(id+"F3.opExtrude","CAP_FACE",FACE,{"disambiguationData":[OSD([sQuery(id+"F2.wireOp",EDGE,"E126.0.0"),sQuery(id+"F2.wireOp",EDGE,"E126.0.1"),sQuery(id+"F2.wireOp",EDGE,"E126.0.3"),sQuery(id+"F2.wireOp",EDGE,"E127.0.0"),sQuery(id+"F2.wireOp",EDGE,"E127.0.1"),sQuery(id+"F2.wireOp",EDGE,"E127.0.3"),sQuery(id+"F2.wireOp",EDGE,"E128.0.0"),sQuery(id+"F2.wireOp",EDGE,"E128.0.1"),sQuery(id+"F2.wireOp",EDGE,"E128.0.3"),sQuery(id+"F2.wireOp",EDGE,"E129.0.0"),sQuery(id+"F2.wireOp",EDGE,"E129.0.1"),sQuery(id+"F2.wireOp",EDGE,"E129.0.3"),sQuery(id+"F2.wireOp",EDGE,"E131.0.0"),sQuery(id+"F2.wireOp",EDGE,"E131.0.1"),sQuery(id+"F2.wireOp",EDGE,"E131.0.3"),sQuery(id+"F2.wireOp",EDGE,"E131.1.0"),sQuery(id+"F2.wireOp",EDGE,"E131.1.1"),sQuery(id+"F2.wireOp",EDGE,"E131.1.3"),sQuery(id+"F2.wireOp",EDGE,"E131.2.0"),sQuery(id+"F2.wireOp",EDGE,"E131.2.1"),sQuery(id+"F2.wireOp",EDGE,"E131.2.3"),sQuery(id+"F2.wireOp",EDGE,"E131.3.0"),sQuery(id+"F2.wireOp",EDGE,"E131.3.1"),sQuery(id+"F2.wireOp",EDGE,"E131.3.3"),sQuery(id+"F2.wireOp",EDGE,"E132"),sQuery(id+"F2.wireOp",EDGE,"E133"),sQuery(id+"F2.wireOp",EDGE,"E134"),sQuery(id+"F2.wireOp",EDGE,"E135"),sQuery(id+"F2.wireOp",EDGE,"E136"),sQuery(id+"F2.wireOp",EDGE,"E137"),sQuery(id+"F2.wireOp",EDGE,"E138"),sQuery(id+"F2.wireOp",EDGE,"Hb3NIat4-kSD9-6Ler-pSma-hnxKwsakkBqM"),sQuery(id+"F2.wireOp",EDGE,"41d37e39-173f-4029-bd79-557eedd61d450.MirrorCS"),sQuery(id+"F2.wireOp",EDGE,"41d37e39-173f-4029-bd79-557eedd61d451.MirrorCS"),sQuery(id+"F2.wireOp",EDGE,"41d37e39-173f-4029-bd79-557eedd61d452.MirrorCS"),sQuery(id+"F2.wireOp",EDGE,"41d37e39-173f-4029-bd79-557eedd61d453.MirrorCS"),sQuery(id+"F2.wireOp",EDGE,"41d37e39-173f-4029-bd79-557eedd61d454.MirrorCS"),sQuery(id+"F2.wireOp",EDGE,"41d37e39-173f-4029-bd79-557eedd61d455.MirrorCS"),sQuery(id+"F2.wireOp",EDGE,"41d37e39-173f-4029-bd79-557eedd61d456.MirrorCS"),sQuery(id+"F2.wireOp",EDGE,"41d37e39-173f-4029-bd79-557eedd61d457.MirrorCS"),sQuery(id+"F2.wireOp",EDGE,"41d37e39-173f-4029-bd79-557eedd61d458.MirrorCS"),sQuery(id+"F2.wireOp",EDGE,"41d37e39-173f-4029-bd79-557eedd61d459.MirrorCS"),sQuery(id+"F2.wireOp",EDGE,"41d37e39-173f-4029-bd79-557eedd61d4510.MirrorCS"),sQuery(id+"F2.wireOp",EDGE,"41d37e39-173f-4029-bd79-557eedd61d4511.MirrorCS"),sQuery(id+"F2.wireOp",EDGE,"41d37e39-173f-4029-bd79-557eedd61d4512.MirrorCS"),sQuery(id+"F2.wireOp",EDGE,"41d37e39-173f-4029-bd79-557eedd61d4513.MirrorCS"),sQuery(id+"F2.wireOp",EDGE,"41d37e39-173f-4029-bd79-557eedd61d4514.MirrorCS"),sQuery(id+"F2.wireOp",EDGE,"41d37e39-173f-4029-bd79-557eedd61d4515.MirrorCS"),sQuery(id+"F2.wireOp",EDGE,"41d37e39-173f-4029-bd79-557eedd61d4516.MirrorCS"),sQuery(id+"F2.wireOp",EDGE,"41d37e39-173f-4029-bd79-557eedd61d4517.MirrorCS"),sQuery(id+"F2.wireOp",EDGE,"41d37e39-173f-4029-bd79-557eedd61d4518.MirrorCS"),sQuery(id+"F2.wireOp",EDGE,"41d37e39-173f-4029-bd79-557eedd61d4519.MirrorCS"),sQuery(id+"F2.wireOp",EDGE,"41d37e39-173f-4029-bd79-557eedd61d4520.MirrorCS"),sQuery(id+"F2.wireOp",EDGE,"41d37e39-173f-4029-bd79-557eedd61d4521.MirrorCS"),sQuery(id+"F2.wireOp",EDGE,"41d37e39-173f-4029-bd79-557eedd61d4522.MirrorCS"),sQuery(id+"F2.wireOp",EDGE,"41d37e39-173f-4029-bd79-557eedd61d4523.MirrorCS"),sQuery(id+"F2.wireOp",EDGE,"523ca1a3-eebf-48df-aab7-9edb756cac68.trimOffspring"),sQuery(id+"F2.wireOp",EDGE,"060e629e-25f2-467f-8377-81ef5d91a4a0.trimOffspring"),sQuery(id+"F2.wireOp",EDGE,"7158a236-c4c9-4158-83ba-993b4190ea9d.trimOffspring"),sQuery(id+"F2.wireOp",EDGE,"92db6ef1-8de9-4aa0-a9a7-105cbcfc27d6.trimOffspring"),sQuery(id+"F2.wireOp",EDGE,"69ba0e40-cee6-4f9a-9526-7aec7b3fb0f5.trimOffspring"),sQuery(id+"F2.wireOp",EDGE,"65cc41be-b745-4d81-9f51-967193abef19.trimOffspring"),sQuery(id+"F2.wireOp",EDGE,"7b3799e5-2319-4c19-9c2a-4c8b996bcf9b.trimOffspring"),sQuery(id+"F2.wireOp",EDGE,"E140"),sQuery(id+"F2.wireOp",EDGE,"E141.MirrorCS"),sQuery(id+"F2.wireOp",EDGE,"E142.MirrorCS"),sQuery(id+"F2.wireOp",EDGE,"E143.MirrorCS"),sQuery(id+"F2.wireOp",EDGE,"E144.MirrorCS"),sQuery(id+"F2.wireOp",EDGE,"E145.MirrorCS"),sQuery(id+"F2.wireOp",EDGE,"E146.MirrorCS"),sQuery(id+"F2.wireOp",EDGE,"E147.MirrorCS"),sQuery(id+"F2.wireOp",EDGE,"E148.MirrorCS"),sQuery(id+"F2.wireOp",EDGE,"E149.MirrorCS"),sQuery(id+"F2.wireOp",EDGE,"E150.MirrorCS"),sQuery(id+"F2.wireOp",EDGE,"E151.MirrorCS"),sQuery(id+"F2.wireOp",EDGE,"E152.MirrorCS"),sQuery(id+"F2.wireOp",EDGE,"E153.MirrorCS"),sQuery(id+"F2.wireOp",EDGE,"E154.MirrorCS"),sQuery(id+"F2.wireOp",EDGE,"E155.MirrorCS"),sQuery(id+"F2.wireOp",EDGE,"E156.MirrorCS"),sQuery(id+"F2.wireOp",EDGE,"E158.MirrorCS"),sQuery(id+"F2.wireOp",EDGE,"E160.MirrorCS"),sQuery(id+"F2.wireOp",EDGE,"E161.MirrorCS"),sQuery(id+"F2.wireOp",EDGE,"E162.MirrorCS"),sQuery(id+"F2.wireOp",EDGE,"E163.MirrorCS"),sQuery(id+"F2.wireOp",EDGE,"E164.trimOffspring"),sQuery(id+"F2.wireOp",EDGE,"E165.trimOffspring"),sQuery(id+"F2.wireOp",EDGE,"E166.trimOffspring"),sQuery(id+"F2.wireOp",EDGE,"E167.trimOffspring"),sQuery(id+"F2.wireOp",EDGE,"E168.trimOffspring"),sQuery(id+"F2.wireOp",EDGE,"E169.trimOffspring"),sQuery(id+"F2.wireOp",EDGE,"E170.trimOffspring"),sQuery(id+"F2.wireOp",EDGE,"E172.MirrorCS"),sQuery(id+"F2.wireOp",EDGE,"E173.MirrorCS"),sQuery(id+"F2.wireOp",EDGE,"E174.MirrorCS"),sQuery(id+"F2.wireOp",EDGE,"E175.MirrorCS"),sQuery(id+"F2.wireOp",EDGE,"E176.MirrorCS"),sQuery(id+"F2.wireOp",EDGE,"E177.MirrorCS"),sQuery(id+"F2.wireOp",EDGE,"E178.MirrorCS"),sQuery(id+"F2.wireOp",EDGE,"E179.MirrorCS"),sQuery(id+"F2.wireOp",EDGE,"E180.MirrorCS"),sQuery(id+"F2.wireOp",EDGE,"E181.MirrorCS"),sQuery(id+"F2.wireOp",EDGE,"E182.MirrorCS"),sQuery(id+"F2.wireOp",EDGE,"E183.MirrorCS"),sQuery(id+"F2.wireOp",EDGE,"E184.MirrorCS"),sQuery(id+"F2.wireOp",EDGE,"E185.MirrorCS"),sQuery(id+"F2.wireOp",EDGE,"E186.MirrorCS"),sQuery(id+"F2.wireOp",EDGE,"E187.MirrorCS"),sQuery(id+"F2.wireOp",EDGE,"E188.MirrorCS"),sQuery(id+"F2.wireOp",EDGE,"E190.MirrorCS"),sQuery(id+"F2.wireOp",EDGE,"E191.MirrorCS"),sQuery(id+"F2.wireOp",EDGE,"E192.MirrorCS"),sQuery(id+"F2.wireOp",EDGE,"E193.MirrorCS"),sQuery(id+"F2.wireOp",EDGE,"E195"),sQuery(id+"F2.wireOp",EDGE,"E196"),sQuery(id+"F2.wireOp",EDGE,"E197"),sQuery(id+"F2.wireOp",EDGE,"E198"),sQuery(id+"F2.wireOp",EDGE,"E199"),sQuery(id+"F2.wireOp",EDGE,"E200"),sQuery(id+"F2.wireOp",EDGE,"E201"),sQuery(id+"F2.wireOp",EDGE,"MxpDbHbz-zyq7-HrCj-Ydf1-zGpcHpEfspLP"),sQuery(id+"F2.wireOp",EDGE,"E202")])],"isStart":true});
            var sketch = newSketch(context, id + "F6", { "sketchPlane" : qUnion([Q0])});
            skLineSegment(sketch, "E279", {"start": v(-135, 171.45) * mm, "end": v(-135, 6.35) * mm, "construction": true});
            skLineSegment(sketch, "E280", {"start": v(-135, 44.45) * mm, "end": v(68.2, 44.45) * mm, "construction": true});
            skLineSegment(sketch, "E281.bottom", {"start": v(-46.1, 47.63) * mm, "end": v(-20.7, 47.63) * mm});
            skLineSegment(sketch, "E281.top", {"start": v(-46.1, 41.28) * mm, "end": v(-20.7, 41.28) * mm});
            skLineSegment(sketch, "E281.left", {"start": v(-46.1, 47.63) * mm, "end": v(-46.1, 41.28) * mm});
            skLineSegment(sketch, "E281.right", {"start": v(-20.7, 47.63) * mm, "end": v(-20.7, 41.28) * mm});
            skPoint(sketch, "E281.middle", {"position": v(-33.4, 44.45) * mm});
            skLineSegment(sketch, "E282.2.0.0", {"start": v(-84.2, 47.63) * mm, "end": v(-84.2, 41.28) * mm});
            skLineSegment(sketch, "E282.3.0.0", {"start": v(-109.6, 47.63) * mm, "end": v(-109.6, 41.28) * mm});
            skLineSegment(sketch, "E283", {"start": v(-109.6, 47.63) * mm, "end": v(-84.2, 47.63) * mm});
            skLineSegment(sketch, "E284", {"start": v(-109.6, 41.28) * mm, "end": v(-84.2, 41.28) * mm});
            skLineSegment(sketch, "E285.bottom", {"start": v(17.4, 47.63) * mm, "end": v(42.8, 47.63) * mm});
            skLineSegment(sketch, "E285.top", {"start": v(17.4, 41.28) * mm, "end": v(42.8, 41.28) * mm});
            skLineSegment(sketch, "E285.left", {"start": v(17.4, 47.63) * mm, "end": v(17.4, 41.28) * mm});
            skLineSegment(sketch, "E285.right", {"start": v(42.8, 47.63) * mm, "end": v(42.8, 41.28) * mm});
            skPoint(sketch, "E285.middle", {"position": v(30.1, 44.45) * mm});
            skSolve(sketch);
        }
        {
            var Q0;
            Q0 = qSketchRegion(id + "F6", true);
            var Q1;
            Q1=makeQuery(id+"F3.opExtrude","CAP_FACE",FACE,{"disambiguationData":[OSD([sQuery(id+"F2.wireOp",EDGE,"E126.0.0"),sQuery(id+"F2.wireOp",EDGE,"E126.0.1"),sQuery(id+"F2.wireOp",EDGE,"E126.0.3"),sQuery(id+"F2.wireOp",EDGE,"E127.0.0"),sQuery(id+"F2.wireOp",EDGE,"E127.0.1"),sQuery(id+"F2.wireOp",EDGE,"E127.0.3"),sQuery(id+"F2.wireOp",EDGE,"E128.0.0"),sQuery(id+"F2.wireOp",EDGE,"E128.0.1"),sQuery(id+"F2.wireOp",EDGE,"E128.0.3"),sQuery(id+"F2.wireOp",EDGE,"E129.0.0"),sQuery(id+"F2.wireOp",EDGE,"E129.0.1"),sQuery(id+"F2.wireOp",EDGE,"E129.0.3"),sQuery(id+"F2.wireOp",EDGE,"E131.0.0"),sQuery(id+"F2.wireOp",EDGE,"E131.0.1"),sQuery(id+"F2.wireOp",EDGE,"E131.0.3"),sQuery(id+"F2.wireOp",EDGE,"E131.1.0"),sQuery(id+"F2.wireOp",EDGE,"E131.1.1"),sQuery(id+"F2.wireOp",EDGE,"E131.1.3"),sQuery(id+"F2.wireOp",EDGE,"E131.2.0"),sQuery(id+"F2.wireOp",EDGE,"E131.2.1"),sQuery(id+"F2.wireOp",EDGE,"E131.2.3"),sQuery(id+"F2.wireOp",EDGE,"E131.3.0"),sQuery(id+"F2.wireOp",EDGE,"E131.3.1"),sQuery(id+"F2.wireOp",EDGE,"E131.3.3"),sQuery(id+"F2.wireOp",EDGE,"E132"),sQuery(id+"F2.wireOp",EDGE,"E133"),sQuery(id+"F2.wireOp",EDGE,"E134"),sQuery(id+"F2.wireOp",EDGE,"E135"),sQuery(id+"F2.wireOp",EDGE,"E136"),sQuery(id+"F2.wireOp",EDGE,"E137"),sQuery(id+"F2.wireOp",EDGE,"E138"),sQuery(id+"F2.wireOp",EDGE,"Hb3NIat4-kSD9-6Ler-pSma-hnxKwsakkBqM"),sQuery(id+"F2.wireOp",EDGE,"41d37e39-173f-4029-bd79-557eedd61d450.MirrorCS"),sQuery(id+"F2.wireOp",EDGE,"41d37e39-173f-4029-bd79-557eedd61d451.MirrorCS"),sQuery(id+"F2.wireOp",EDGE,"41d37e39-173f-4029-bd79-557eedd61d452.MirrorCS"),sQuery(id+"F2.wireOp",EDGE,"41d37e39-173f-4029-bd79-557eedd61d453.MirrorCS"),sQuery(id+"F2.wireOp",EDGE,"41d37e39-173f-4029-bd79-557eedd61d454.MirrorCS"),sQuery(id+"F2.wireOp",EDGE,"41d37e39-173f-4029-bd79-557eedd61d455.MirrorCS"),sQuery(id+"F2.wireOp",EDGE,"41d37e39-173f-4029-bd79-557eedd61d456.MirrorCS"),sQuery(id+"F2.wireOp",EDGE,"41d37e39-173f-4029-bd79-557eedd61d457.MirrorCS"),sQuery(id+"F2.wireOp",EDGE,"41d37e39-173f-4029-bd79-557eedd61d458.MirrorCS"),sQuery(id+"F2.wireOp",EDGE,"41d37e39-173f-4029-bd79-557eedd61d459.MirrorCS"),sQuery(id+"F2.wireOp",EDGE,"41d37e39-173f-4029-bd79-557eedd61d4510.MirrorCS"),sQuery(id+"F2.wireOp",EDGE,"41d37e39-173f-4029-bd79-557eedd61d4511.MirrorCS"),sQuery(id+"F2.wireOp",EDGE,"41d37e39-173f-4029-bd79-557eedd61d4512.MirrorCS"),sQuery(id+"F2.wireOp",EDGE,"41d37e39-173f-4029-bd79-557eedd61d4513.MirrorCS"),sQuery(id+"F2.wireOp",EDGE,"41d37e39-173f-4029-bd79-557eedd61d4514.MirrorCS"),sQuery(id+"F2.wireOp",EDGE,"41d37e39-173f-4029-bd79-557eedd61d4515.MirrorCS"),sQuery(id+"F2.wireOp",EDGE,"41d37e39-173f-4029-bd79-557eedd61d4516.MirrorCS"),sQuery(id+"F2.wireOp",EDGE,"41d37e39-173f-4029-bd79-557eedd61d4517.MirrorCS"),sQuery(id+"F2.wireOp",EDGE,"41d37e39-173f-4029-bd79-557eedd61d4518.MirrorCS"),sQuery(id+"F2.wireOp",EDGE,"41d37e39-173f-4029-bd79-557eedd61d4519.MirrorCS"),sQuery(id+"F2.wireOp",EDGE,"41d37e39-173f-4029-bd79-557eedd61d4520.MirrorCS"),sQuery(id+"F2.wireOp",EDGE,"41d37e39-173f-4029-bd79-557eedd61d4521.MirrorCS"),sQuery(id+"F2.wireOp",EDGE,"41d37e39-173f-4029-bd79-557eedd61d4522.MirrorCS"),sQuery(id+"F2.wireOp",EDGE,"41d37e39-173f-4029-bd79-557eedd61d4523.MirrorCS"),sQuery(id+"F2.wireOp",EDGE,"523ca1a3-eebf-48df-aab7-9edb756cac68.trimOffspring"),sQuery(id+"F2.wireOp",EDGE,"060e629e-25f2-467f-8377-81ef5d91a4a0.trimOffspring"),sQuery(id+"F2.wireOp",EDGE,"7158a236-c4c9-4158-83ba-993b4190ea9d.trimOffspring"),sQuery(id+"F2.wireOp",EDGE,"92db6ef1-8de9-4aa0-a9a7-105cbcfc27d6.trimOffspring"),sQuery(id+"F2.wireOp",EDGE,"69ba0e40-cee6-4f9a-9526-7aec7b3fb0f5.trimOffspring"),sQuery(id+"F2.wireOp",EDGE,"65cc41be-b745-4d81-9f51-967193abef19.trimOffspring"),sQuery(id+"F2.wireOp",EDGE,"7b3799e5-2319-4c19-9c2a-4c8b996bcf9b.trimOffspring"),sQuery(id+"F2.wireOp",EDGE,"E140"),sQuery(id+"F2.wireOp",EDGE,"E141.MirrorCS"),sQuery(id+"F2.wireOp",EDGE,"E142.MirrorCS"),sQuery(id+"F2.wireOp",EDGE,"E143.MirrorCS"),sQuery(id+"F2.wireOp",EDGE,"E144.MirrorCS"),sQuery(id+"F2.wireOp",EDGE,"E145.MirrorCS"),sQuery(id+"F2.wireOp",EDGE,"E146.MirrorCS"),sQuery(id+"F2.wireOp",EDGE,"E147.MirrorCS"),sQuery(id+"F2.wireOp",EDGE,"E148.MirrorCS"),sQuery(id+"F2.wireOp",EDGE,"E149.MirrorCS"),sQuery(id+"F2.wireOp",EDGE,"E150.MirrorCS"),sQuery(id+"F2.wireOp",EDGE,"E151.MirrorCS"),sQuery(id+"F2.wireOp",EDGE,"E152.MirrorCS"),sQuery(id+"F2.wireOp",EDGE,"E153.MirrorCS"),sQuery(id+"F2.wireOp",EDGE,"E154.MirrorCS"),sQuery(id+"F2.wireOp",EDGE,"E155.MirrorCS"),sQuery(id+"F2.wireOp",EDGE,"E156.MirrorCS"),sQuery(id+"F2.wireOp",EDGE,"E158.MirrorCS"),sQuery(id+"F2.wireOp",EDGE,"E160.MirrorCS"),sQuery(id+"F2.wireOp",EDGE,"E161.MirrorCS"),sQuery(id+"F2.wireOp",EDGE,"E162.MirrorCS"),sQuery(id+"F2.wireOp",EDGE,"E163.MirrorCS"),sQuery(id+"F2.wireOp",EDGE,"E164.trimOffspring"),sQuery(id+"F2.wireOp",EDGE,"E165.trimOffspring"),sQuery(id+"F2.wireOp",EDGE,"E166.trimOffspring"),sQuery(id+"F2.wireOp",EDGE,"E167.trimOffspring"),sQuery(id+"F2.wireOp",EDGE,"E168.trimOffspring"),sQuery(id+"F2.wireOp",EDGE,"E169.trimOffspring"),sQuery(id+"F2.wireOp",EDGE,"E170.trimOffspring"),sQuery(id+"F2.wireOp",EDGE,"E172.MirrorCS"),sQuery(id+"F2.wireOp",EDGE,"E173.MirrorCS"),sQuery(id+"F2.wireOp",EDGE,"E174.MirrorCS"),sQuery(id+"F2.wireOp",EDGE,"E175.MirrorCS"),sQuery(id+"F2.wireOp",EDGE,"E176.MirrorCS"),sQuery(id+"F2.wireOp",EDGE,"E177.MirrorCS"),sQuery(id+"F2.wireOp",EDGE,"E178.MirrorCS"),sQuery(id+"F2.wireOp",EDGE,"E179.MirrorCS"),sQuery(id+"F2.wireOp",EDGE,"E180.MirrorCS"),sQuery(id+"F2.wireOp",EDGE,"E181.MirrorCS"),sQuery(id+"F2.wireOp",EDGE,"E182.MirrorCS"),sQuery(id+"F2.wireOp",EDGE,"E183.MirrorCS"),sQuery(id+"F2.wireOp",EDGE,"E184.MirrorCS"),sQuery(id+"F2.wireOp",EDGE,"E185.MirrorCS"),sQuery(id+"F2.wireOp",EDGE,"E186.MirrorCS"),sQuery(id+"F2.wireOp",EDGE,"E187.MirrorCS"),sQuery(id+"F2.wireOp",EDGE,"E188.MirrorCS"),sQuery(id+"F2.wireOp",EDGE,"E190.MirrorCS"),sQuery(id+"F2.wireOp",EDGE,"E191.MirrorCS"),sQuery(id+"F2.wireOp",EDGE,"E192.MirrorCS"),sQuery(id+"F2.wireOp",EDGE,"E193.MirrorCS"),sQuery(id+"F2.wireOp",EDGE,"E195"),sQuery(id+"F2.wireOp",EDGE,"E196"),sQuery(id+"F2.wireOp",EDGE,"E197"),sQuery(id+"F2.wireOp",EDGE,"E198"),sQuery(id+"F2.wireOp",EDGE,"E199"),sQuery(id+"F2.wireOp",EDGE,"E200"),sQuery(id+"F2.wireOp",EDGE,"E201"),sQuery(id+"F2.wireOp",EDGE,"MxpDbHbz-zyq7-HrCj-Ydf1-zGpcHpEfspLP"),sQuery(id+"F2.wireOp",EDGE,"E202")])],"isStart":false});
            extrude(context, id + "F7", {"entities" : qUnion([Q0]), "operationType" : NewBodyOperationType.REMOVE, "endBound" : BoundingType.UP_TO_SURFACE, "oppositeDirection" : true, "depth" : 25.4 * mm, "endBoundEntityFace" : qUnion([Q1]), "offsetDistance" : 25.4 * mm});
        }
        {
            var Q0;
            Q0=makeQuery(id+"F5.opExtrude","CAP_FACE",FACE,{"disambiguationData":[OSD([sQuery(id+"F4.wireOp",EDGE,"E208.0.0"),sQuery(id+"F4.wireOp",EDGE,"E208.0.1"),sQuery(id+"F4.wireOp",EDGE,"E208.0.3"),sQuery(id+"F4.wireOp",EDGE,"E209.0.0"),sQuery(id+"F4.wireOp",EDGE,"E209.0.1"),sQuery(id+"F4.wireOp",EDGE,"E209.0.3"),sQuery(id+"F4.wireOp",EDGE,"E210.0.0"),sQuery(id+"F4.wireOp",EDGE,"E210.0.1"),sQuery(id+"F4.wireOp",EDGE,"E210.0.3"),sQuery(id+"F4.wireOp",EDGE,"E211.0.0"),sQuery(id+"F4.wireOp",EDGE,"E211.0.1"),sQuery(id+"F4.wireOp",EDGE,"E211.0.3"),sQuery(id+"F4.wireOp",EDGE,"E212.0.0"),sQuery(id+"F4.wireOp",EDGE,"E212.0.1"),sQuery(id+"F4.wireOp",EDGE,"E212.0.3"),sQuery(id+"F4.wireOp",EDGE,"E213.0.0"),sQuery(id+"F4.wireOp",EDGE,"E213.0.1"),sQuery(id+"F4.wireOp",EDGE,"E213.0.3"),sQuery(id+"F4.wireOp",EDGE,"E214.0.0"),sQuery(id+"F4.wireOp",EDGE,"E214.0.1"),sQuery(id+"F4.wireOp",EDGE,"E214.0.3"),sQuery(id+"F4.wireOp",EDGE,"E215.0.0"),sQuery(id+"F4.wireOp",EDGE,"E215.0.1"),sQuery(id+"F4.wireOp",EDGE,"E215.0.3"),sQuery(id+"F4.wireOp",EDGE,"E216.0.1"),sQuery(id+"F4.wireOp",EDGE,"E216.0.2"),sQuery(id+"F4.wireOp",EDGE,"E216.0.3"),sQuery(id+"F4.wireOp",EDGE,"E217.0.1"),sQuery(id+"F4.wireOp",EDGE,"E217.0.2"),sQuery(id+"F4.wireOp",EDGE,"E217.0.3"),sQuery(id+"F4.wireOp",EDGE,"E218.0.1"),sQuery(id+"F4.wireOp",EDGE,"E218.0.2"),sQuery(id+"F4.wireOp",EDGE,"E218.0.3"),sQuery(id+"F4.wireOp",EDGE,"E219.0.1"),sQuery(id+"F4.wireOp",EDGE,"E219.0.2"),sQuery(id+"F4.wireOp",EDGE,"E219.0.3"),sQuery(id+"F4.wireOp",EDGE,"E220.0.1"),sQuery(id+"F4.wireOp",EDGE,"E220.0.2"),sQuery(id+"F4.wireOp",EDGE,"E220.0.3"),sQuery(id+"F4.wireOp",EDGE,"E221.0.1"),sQuery(id+"F4.wireOp",EDGE,"E221.0.2"),sQuery(id+"F4.wireOp",EDGE,"E221.0.3"),sQuery(id+"F4.wireOp",EDGE,"E222.0.1"),sQuery(id+"F4.wireOp",EDGE,"E222.0.2"),sQuery(id+"F4.wireOp",EDGE,"E222.0.3"),sQuery(id+"F4.wireOp",EDGE,"E223"),sQuery(id+"F4.wireOp",EDGE,"E224"),sQuery(id+"F4.wireOp",EDGE,"E225"),sQuery(id+"F4.wireOp",EDGE,"E226"),sQuery(id+"F4.wireOp",EDGE,"E227"),sQuery(id+"F4.wireOp",EDGE,"E228"),sQuery(id+"F4.wireOp",EDGE,"E229"),sQuery(id+"F4.wireOp",EDGE,"E230"),sQuery(id+"F4.wireOp",EDGE,"E231"),sQuery(id+"F4.wireOp",EDGE,"E232"),sQuery(id+"F4.wireOp",EDGE,"E233"),sQuery(id+"F4.wireOp",EDGE,"E234"),sQuery(id+"F4.wireOp",EDGE,"E235"),sQuery(id+"F4.wireOp",EDGE,"E236"),sQuery(id+"F4.wireOp",EDGE,"E237"),sQuery(id+"F4.wireOp",EDGE,"E240.MirrorCS"),sQuery(id+"F4.wireOp",EDGE,"E241.MirrorCS"),sQuery(id+"F4.wireOp",EDGE,"E242.MirrorCS"),sQuery(id+"F4.wireOp",EDGE,"E243.MirrorCS"),sQuery(id+"F4.wireOp",EDGE,"E244.MirrorCS"),sQuery(id+"F4.wireOp",EDGE,"E245.MirrorCS"),sQuery(id+"F4.wireOp",EDGE,"E246.MirrorCS"),sQuery(id+"F4.wireOp",EDGE,"E247.MirrorCS"),sQuery(id+"F4.wireOp",EDGE,"E248.MirrorCS"),sQuery(id+"F4.wireOp",EDGE,"E249.MirrorCS"),sQuery(id+"F4.wireOp",EDGE,"E250.MirrorCS"),sQuery(id+"F4.wireOp",EDGE,"E251.MirrorCS"),sQuery(id+"F4.wireOp",EDGE,"E252.MirrorCS"),sQuery(id+"F4.wireOp",EDGE,"E253.MirrorCS"),sQuery(id+"F4.wireOp",EDGE,"E254.MirrorCS"),sQuery(id+"F4.wireOp",EDGE,"E255.MirrorCS"),sQuery(id+"F4.wireOp",EDGE,"E256.MirrorCS"),sQuery(id+"F4.wireOp",EDGE,"E257.MirrorCS"),sQuery(id+"F4.wireOp",EDGE,"E258.MirrorCS"),sQuery(id+"F4.wireOp",EDGE,"E259.MirrorCS"),sQuery(id+"F4.wireOp",EDGE,"E260.MirrorCS"),sQuery(id+"F4.wireOp",EDGE,"E261.MirrorCS"),sQuery(id+"F4.wireOp",EDGE,"E262.MirrorCS"),sQuery(id+"F4.wireOp",EDGE,"E263.MirrorCS"),sQuery(id+"F4.wireOp",EDGE,"E264.MirrorCS"),sQuery(id+"F4.wireOp",EDGE,"E265.MirrorCS"),sQuery(id+"F4.wireOp",EDGE,"E266.MirrorCS"),sQuery(id+"F4.wireOp",EDGE,"E267.MirrorCS"),sQuery(id+"F4.wireOp",EDGE,"E268.MirrorCS"),sQuery(id+"F4.wireOp",EDGE,"d03f6234-f1c8-4994-bb03-d69cd6cd5b271.MirrorCS"),sQuery(id+"F4.wireOp",EDGE,"d03f6234-f1c8-4994-bb03-d69cd6cd5b273.MirrorCS"),sQuery(id+"F4.wireOp",EDGE,"d03f6234-f1c8-4994-bb03-d69cd6cd5b274.MirrorCS"),sQuery(id+"F4.wireOp",EDGE,"d03f6234-f1c8-4994-bb03-d69cd6cd5b275.MirrorCS"),sQuery(id+"F4.wireOp",EDGE,"d03f6234-f1c8-4994-bb03-d69cd6cd5b276.MirrorCS"),sQuery(id+"F4.wireOp",EDGE,"d03f6234-f1c8-4994-bb03-d69cd6cd5b277.MirrorCS"),sQuery(id+"F4.wireOp",EDGE,"d03f6234-f1c8-4994-bb03-d69cd6cd5b278.MirrorCS"),sQuery(id+"F4.wireOp",EDGE,"d03f6234-f1c8-4994-bb03-d69cd6cd5b279.MirrorCS"),sQuery(id+"F4.wireOp",EDGE,"d03f6234-f1c8-4994-bb03-d69cd6cd5b2710.MirrorCS"),sQuery(id+"F4.wireOp",EDGE,"d03f6234-f1c8-4994-bb03-d69cd6cd5b2711.MirrorCS"),sQuery(id+"F4.wireOp",EDGE,"d03f6234-f1c8-4994-bb03-d69cd6cd5b2712.MirrorCS"),sQuery(id+"F4.wireOp",EDGE,"d03f6234-f1c8-4994-bb03-d69cd6cd5b2713.MirrorCS"),sQuery(id+"F4.wireOp",EDGE,"d03f6234-f1c8-4994-bb03-d69cd6cd5b2714.MirrorCS"),sQuery(id+"F4.wireOp",EDGE,"d03f6234-f1c8-4994-bb03-d69cd6cd5b2715.MirrorCS"),sQuery(id+"F4.wireOp",EDGE,"d03f6234-f1c8-4994-bb03-d69cd6cd5b2716.MirrorCS"),sQuery(id+"F4.wireOp",EDGE,"d03f6234-f1c8-4994-bb03-d69cd6cd5b2717.MirrorCS"),sQuery(id+"F4.wireOp",EDGE,"d03f6234-f1c8-4994-bb03-d69cd6cd5b2718.MirrorCS"),sQuery(id+"F4.wireOp",EDGE,"d03f6234-f1c8-4994-bb03-d69cd6cd5b2719.MirrorCS"),sQuery(id+"F4.wireOp",EDGE,"E2710.MirrorCS"),sQuery(id+"F4.wireOp",EDGE,"E2712.MirrorCS"),sQuery(id+"F4.wireOp",EDGE,"E2714.MirrorCS"),sQuery(id+"F4.wireOp",EDGE,"E2715.MirrorCS"),sQuery(id+"F4.wireOp",EDGE,"E2716.MirrorCS"),sQuery(id+"F4.wireOp",EDGE,"E2718.MirrorCS"),sQuery(id+"F4.wireOp",EDGE,"E2719.MirrorCS"),sQuery(id+"F4.wireOp",EDGE,"d03f6234-f1c8-4994-bb03-d69cd6cd5b2730.MirrorCS"),sQuery(id+"F4.wireOp",EDGE,"d03f6234-f1c8-4994-bb03-d69cd6cd5b2731.MirrorCS"),sQuery(id+"F4.wireOp",EDGE,"d03f6234-f1c8-4994-bb03-d69cd6cd5b2732.MirrorCS"),sQuery(id+"F4.wireOp",EDGE,"d03f6234-f1c8-4994-bb03-d69cd6cd5b2733.MirrorCS"),sQuery(id+"F4.wireOp",EDGE,"d03f6234-f1c8-4994-bb03-d69cd6cd5b2734.MirrorCS"),sQuery(id+"F4.wireOp",EDGE,"d03f6234-f1c8-4994-bb03-d69cd6cd5b2735.MirrorCS"),sQuery(id+"F4.wireOp",EDGE,"d03f6234-f1c8-4994-bb03-d69cd6cd5b2736.MirrorCS"),sQuery(id+"F4.wireOp",EDGE,"d03f6234-f1c8-4994-bb03-d69cd6cd5b2737.MirrorCS")])],"isStart":true});
            var sketch = newSketch(context, id + "F8", { "sketchPlane" : qUnion([Q0])});
            skLineSegment(sketch, "E286", {"start": v(106.5, 184.15) * mm, "end": v(103.32, 6.35) * mm, "construction": true});
            skLineSegment(sketch, "E287", {"start": v(-99.88, 184.15) * mm, "end": v(-99.88, 6.35) * mm, "construction": true});
            skLineSegment(sketch, "E288", {"start": v(-99.88, 44.45) * mm, "end": v(104, 44.45) * mm, "construction": true});
            skLineSegment(sketch, "E289.bottom", {"start": v(-10.64, 47.62) * mm, "end": v(14.76, 47.62) * mm});
            skLineSegment(sketch, "E289.top", {"start": v(-10.64, 41.27) * mm, "end": v(14.76, 41.27) * mm});
            skLineSegment(sketch, "E289.left", {"start": v(-10.64, 47.62) * mm, "end": v(-10.64, 41.27) * mm});
            skLineSegment(sketch, "E289.right", {"start": v(14.76, 47.62) * mm, "end": v(14.76, 41.27) * mm});
            skPoint(sketch, "E289.middle", {"position": v(2.06, 44.45) * mm});
            skLineSegment(sketch, "E290.bottom", {"start": v(-74.14, 47.63) * mm, "end": v(-48.74, 47.63) * mm});
            skLineSegment(sketch, "E290.top", {"start": v(-74.14, 41.28) * mm, "end": v(-48.74, 41.28) * mm});
            skLineSegment(sketch, "E290.left", {"start": v(-74.14, 47.63) * mm, "end": v(-74.14, 41.28) * mm});
            skLineSegment(sketch, "E290.right", {"start": v(-48.74, 47.63) * mm, "end": v(-48.74, 41.28) * mm});
            skPoint(sketch, "E290.middle", {"position": v(-61.44, 44.45) * mm});
            skLineSegment(sketch, "E291.bottom", {"start": v(52.86, 47.63) * mm, "end": v(78.26, 47.63) * mm});
            skLineSegment(sketch, "E291.top", {"start": v(52.86, 41.28) * mm, "end": v(78.26, 41.28) * mm});
            skLineSegment(sketch, "E291.left", {"start": v(52.86, 47.63) * mm, "end": v(52.86, 41.28) * mm});
            skLineSegment(sketch, "E291.right", {"start": v(78.26, 47.63) * mm, "end": v(78.26, 41.28) * mm});
            skPoint(sketch, "E291.middle", {"position": v(65.56, 44.45) * mm});
            skSolve(sketch);
        }
        {
            var Q0;
            Q0 = qSketchRegion(id + "F8", true);
            var Q1;
            Q1=makeQuery(id+"F5.opExtrude","CAP_FACE",FACE,{"disambiguationData":[OSD([sQuery(id+"F4.wireOp",EDGE,"E208.0.0"),sQuery(id+"F4.wireOp",EDGE,"E208.0.1"),sQuery(id+"F4.wireOp",EDGE,"E208.0.3"),sQuery(id+"F4.wireOp",EDGE,"E209.0.0"),sQuery(id+"F4.wireOp",EDGE,"E209.0.1"),sQuery(id+"F4.wireOp",EDGE,"E209.0.3"),sQuery(id+"F4.wireOp",EDGE,"E210.0.0"),sQuery(id+"F4.wireOp",EDGE,"E210.0.1"),sQuery(id+"F4.wireOp",EDGE,"E210.0.3"),sQuery(id+"F4.wireOp",EDGE,"E211.0.0"),sQuery(id+"F4.wireOp",EDGE,"E211.0.1"),sQuery(id+"F4.wireOp",EDGE,"E211.0.3"),sQuery(id+"F4.wireOp",EDGE,"E212.0.0"),sQuery(id+"F4.wireOp",EDGE,"E212.0.1"),sQuery(id+"F4.wireOp",EDGE,"E212.0.3"),sQuery(id+"F4.wireOp",EDGE,"E213.0.0"),sQuery(id+"F4.wireOp",EDGE,"E213.0.1"),sQuery(id+"F4.wireOp",EDGE,"E213.0.3"),sQuery(id+"F4.wireOp",EDGE,"E214.0.0"),sQuery(id+"F4.wireOp",EDGE,"E214.0.1"),sQuery(id+"F4.wireOp",EDGE,"E214.0.3"),sQuery(id+"F4.wireOp",EDGE,"E215.0.0"),sQuery(id+"F4.wireOp",EDGE,"E215.0.1"),sQuery(id+"F4.wireOp",EDGE,"E215.0.3"),sQuery(id+"F4.wireOp",EDGE,"E216.0.1"),sQuery(id+"F4.wireOp",EDGE,"E216.0.2"),sQuery(id+"F4.wireOp",EDGE,"E216.0.3"),sQuery(id+"F4.wireOp",EDGE,"E217.0.1"),sQuery(id+"F4.wireOp",EDGE,"E217.0.2"),sQuery(id+"F4.wireOp",EDGE,"E217.0.3"),sQuery(id+"F4.wireOp",EDGE,"E218.0.1"),sQuery(id+"F4.wireOp",EDGE,"E218.0.2"),sQuery(id+"F4.wireOp",EDGE,"E218.0.3"),sQuery(id+"F4.wireOp",EDGE,"E219.0.1"),sQuery(id+"F4.wireOp",EDGE,"E219.0.2"),sQuery(id+"F4.wireOp",EDGE,"E219.0.3"),sQuery(id+"F4.wireOp",EDGE,"E220.0.1"),sQuery(id+"F4.wireOp",EDGE,"E220.0.2"),sQuery(id+"F4.wireOp",EDGE,"E220.0.3"),sQuery(id+"F4.wireOp",EDGE,"E221.0.1"),sQuery(id+"F4.wireOp",EDGE,"E221.0.2"),sQuery(id+"F4.wireOp",EDGE,"E221.0.3"),sQuery(id+"F4.wireOp",EDGE,"E222.0.1"),sQuery(id+"F4.wireOp",EDGE,"E222.0.2"),sQuery(id+"F4.wireOp",EDGE,"E222.0.3"),sQuery(id+"F4.wireOp",EDGE,"E223"),sQuery(id+"F4.wireOp",EDGE,"E224"),sQuery(id+"F4.wireOp",EDGE,"E225"),sQuery(id+"F4.wireOp",EDGE,"E226"),sQuery(id+"F4.wireOp",EDGE,"E227"),sQuery(id+"F4.wireOp",EDGE,"E228"),sQuery(id+"F4.wireOp",EDGE,"E229"),sQuery(id+"F4.wireOp",EDGE,"E230"),sQuery(id+"F4.wireOp",EDGE,"E231"),sQuery(id+"F4.wireOp",EDGE,"E232"),sQuery(id+"F4.wireOp",EDGE,"E233"),sQuery(id+"F4.wireOp",EDGE,"E234"),sQuery(id+"F4.wireOp",EDGE,"E235"),sQuery(id+"F4.wireOp",EDGE,"E236"),sQuery(id+"F4.wireOp",EDGE,"E237"),sQuery(id+"F4.wireOp",EDGE,"E240.MirrorCS"),sQuery(id+"F4.wireOp",EDGE,"E241.MirrorCS"),sQuery(id+"F4.wireOp",EDGE,"E242.MirrorCS"),sQuery(id+"F4.wireOp",EDGE,"E243.MirrorCS"),sQuery(id+"F4.wireOp",EDGE,"E244.MirrorCS"),sQuery(id+"F4.wireOp",EDGE,"E245.MirrorCS"),sQuery(id+"F4.wireOp",EDGE,"E246.MirrorCS"),sQuery(id+"F4.wireOp",EDGE,"E247.MirrorCS"),sQuery(id+"F4.wireOp",EDGE,"E248.MirrorCS"),sQuery(id+"F4.wireOp",EDGE,"E249.MirrorCS"),sQuery(id+"F4.wireOp",EDGE,"E250.MirrorCS"),sQuery(id+"F4.wireOp",EDGE,"E251.MirrorCS"),sQuery(id+"F4.wireOp",EDGE,"E252.MirrorCS"),sQuery(id+"F4.wireOp",EDGE,"E253.MirrorCS"),sQuery(id+"F4.wireOp",EDGE,"E254.MirrorCS"),sQuery(id+"F4.wireOp",EDGE,"E255.MirrorCS"),sQuery(id+"F4.wireOp",EDGE,"E256.MirrorCS"),sQuery(id+"F4.wireOp",EDGE,"E257.MirrorCS"),sQuery(id+"F4.wireOp",EDGE,"E258.MirrorCS"),sQuery(id+"F4.wireOp",EDGE,"E259.MirrorCS"),sQuery(id+"F4.wireOp",EDGE,"E260.MirrorCS"),sQuery(id+"F4.wireOp",EDGE,"E261.MirrorCS"),sQuery(id+"F4.wireOp",EDGE,"E262.MirrorCS"),sQuery(id+"F4.wireOp",EDGE,"E263.MirrorCS"),sQuery(id+"F4.wireOp",EDGE,"E264.MirrorCS"),sQuery(id+"F4.wireOp",EDGE,"E265.MirrorCS"),sQuery(id+"F4.wireOp",EDGE,"E266.MirrorCS"),sQuery(id+"F4.wireOp",EDGE,"E267.MirrorCS"),sQuery(id+"F4.wireOp",EDGE,"E268.MirrorCS"),sQuery(id+"F4.wireOp",EDGE,"d03f6234-f1c8-4994-bb03-d69cd6cd5b271.MirrorCS"),sQuery(id+"F4.wireOp",EDGE,"d03f6234-f1c8-4994-bb03-d69cd6cd5b273.MirrorCS"),sQuery(id+"F4.wireOp",EDGE,"d03f6234-f1c8-4994-bb03-d69cd6cd5b274.MirrorCS"),sQuery(id+"F4.wireOp",EDGE,"d03f6234-f1c8-4994-bb03-d69cd6cd5b275.MirrorCS"),sQuery(id+"F4.wireOp",EDGE,"d03f6234-f1c8-4994-bb03-d69cd6cd5b276.MirrorCS"),sQuery(id+"F4.wireOp",EDGE,"d03f6234-f1c8-4994-bb03-d69cd6cd5b277.MirrorCS"),sQuery(id+"F4.wireOp",EDGE,"d03f6234-f1c8-4994-bb03-d69cd6cd5b278.MirrorCS"),sQuery(id+"F4.wireOp",EDGE,"d03f6234-f1c8-4994-bb03-d69cd6cd5b279.MirrorCS"),sQuery(id+"F4.wireOp",EDGE,"d03f6234-f1c8-4994-bb03-d69cd6cd5b2710.MirrorCS"),sQuery(id+"F4.wireOp",EDGE,"d03f6234-f1c8-4994-bb03-d69cd6cd5b2711.MirrorCS"),sQuery(id+"F4.wireOp",EDGE,"d03f6234-f1c8-4994-bb03-d69cd6cd5b2712.MirrorCS"),sQuery(id+"F4.wireOp",EDGE,"d03f6234-f1c8-4994-bb03-d69cd6cd5b2713.MirrorCS"),sQuery(id+"F4.wireOp",EDGE,"d03f6234-f1c8-4994-bb03-d69cd6cd5b2714.MirrorCS"),sQuery(id+"F4.wireOp",EDGE,"d03f6234-f1c8-4994-bb03-d69cd6cd5b2715.MirrorCS"),sQuery(id+"F4.wireOp",EDGE,"d03f6234-f1c8-4994-bb03-d69cd6cd5b2716.MirrorCS"),sQuery(id+"F4.wireOp",EDGE,"d03f6234-f1c8-4994-bb03-d69cd6cd5b2717.MirrorCS"),sQuery(id+"F4.wireOp",EDGE,"d03f6234-f1c8-4994-bb03-d69cd6cd5b2718.MirrorCS"),sQuery(id+"F4.wireOp",EDGE,"d03f6234-f1c8-4994-bb03-d69cd6cd5b2719.MirrorCS"),sQuery(id+"F4.wireOp",EDGE,"E2710.MirrorCS"),sQuery(id+"F4.wireOp",EDGE,"E2712.MirrorCS"),sQuery(id+"F4.wireOp",EDGE,"E2714.MirrorCS"),sQuery(id+"F4.wireOp",EDGE,"E2715.MirrorCS"),sQuery(id+"F4.wireOp",EDGE,"E2716.MirrorCS"),sQuery(id+"F4.wireOp",EDGE,"E2718.MirrorCS"),sQuery(id+"F4.wireOp",EDGE,"E2719.MirrorCS"),sQuery(id+"F4.wireOp",EDGE,"d03f6234-f1c8-4994-bb03-d69cd6cd5b2730.MirrorCS"),sQuery(id+"F4.wireOp",EDGE,"d03f6234-f1c8-4994-bb03-d69cd6cd5b2731.MirrorCS"),sQuery(id+"F4.wireOp",EDGE,"d03f6234-f1c8-4994-bb03-d69cd6cd5b2732.MirrorCS"),sQuery(id+"F4.wireOp",EDGE,"d03f6234-f1c8-4994-bb03-d69cd6cd5b2733.MirrorCS"),sQuery(id+"F4.wireOp",EDGE,"d03f6234-f1c8-4994-bb03-d69cd6cd5b2734.MirrorCS"),sQuery(id+"F4.wireOp",EDGE,"d03f6234-f1c8-4994-bb03-d69cd6cd5b2735.MirrorCS"),sQuery(id+"F4.wireOp",EDGE,"d03f6234-f1c8-4994-bb03-d69cd6cd5b2736.MirrorCS"),sQuery(id+"F4.wireOp",EDGE,"d03f6234-f1c8-4994-bb03-d69cd6cd5b2737.MirrorCS")])],"isStart":false});
            extrude(context, id + "F9", {"entities" : qUnion([Q0]), "operationType" : NewBodyOperationType.REMOVE, "endBound" : BoundingType.UP_TO_SURFACE, "oppositeDirection" : true, "depth" : 25.4 * mm, "endBoundEntityFace" : qUnion([Q1]), "offsetDistance" : 25.4 * mm});
        }
        {
            var Q0;
            Q0=makeQuery(id+"F7.boolean.opBoolean","COPY",FACE,{"derivedFrom":makeQuery(id+"F7.opExtrude","SWEPT_FACE",FACE,{"disambiguationData":[OSD([sQuery(id+"F6.wireOp",EDGE,"E285.top")])]})});
            var sketch = newSketch(context, id + "F10", { "sketchPlane" : qUnion([Q0])});
            skLineSegment(sketch, "E292.0.0", {"start": v(-17.4, -106.23) * mm, "end": v(-17.4, -99.88) * mm});
            skLineSegment(sketch, "E292.0.2", {"start": v(-42.8, -99.88) * mm, "end": v(-42.8, -106.23) * mm});
            skLineSegment(sketch, "E292.0.3", {"start": v(-42.8, -106.23) * mm, "end": v(-17.4, -106.23) * mm});
            skLineSegment(sketch, "E293.0.0", {"start": v(46.1, -106.23) * mm, "end": v(46.1, -99.88) * mm});
            skLineSegment(sketch, "E293.0.2", {"start": v(20.7, -99.88) * mm, "end": v(20.7, -106.23) * mm});
            skLineSegment(sketch, "E293.0.3", {"start": v(20.7, -106.23) * mm, "end": v(46.1, -106.23) * mm});
            skLineSegment(sketch, "E294.0.0", {"start": v(109.6, -106.23) * mm, "end": v(109.6, -99.88) * mm});
            skLineSegment(sketch, "E294.0.2", {"start": v(84.2, -99.88) * mm, "end": v(84.2, -106.23) * mm});
            skLineSegment(sketch, "E294.0.3", {"start": v(84.2, -106.23) * mm, "end": v(109.6, -106.23) * mm});
            skLineSegment(sketch, "E295.0.0", {"start": v(-74.56, -74.14) * mm, "end": v(-68.2, -74.14) * mm});
            skLineSegment(sketch, "E295.0.2", {"start": v(-68.2, -48.74) * mm, "end": v(-74.56, -48.74) * mm});
            skLineSegment(sketch, "E295.0.3", {"start": v(-74.56, -48.74) * mm, "end": v(-74.56, -74.14) * mm});
            skLineSegment(sketch, "E296.0.0", {"start": v(-74.56, -10.64) * mm, "end": v(-68.2, -10.64) * mm});
            skLineSegment(sketch, "E296.0.2", {"start": v(-68.2, 14.76) * mm, "end": v(-74.56, 14.76) * mm});
            skLineSegment(sketch, "E296.0.3", {"start": v(-74.56, 14.76) * mm, "end": v(-74.56, -10.64) * mm});
            skLineSegment(sketch, "E297.0.0", {"start": v(-74.56, 52.86) * mm, "end": v(-68.2, 52.86) * mm});
            skLineSegment(sketch, "E297.0.2", {"start": v(-68.2, 78.26) * mm, "end": v(-74.56, 78.26) * mm});
            skLineSegment(sketch, "E297.0.3", {"start": v(-74.56, 78.26) * mm, "end": v(-74.56, 52.86) * mm});
            skPoint(sketch, "E298.0", {"position": v(-68.2, -99.88) * mm});
            skLineSegment(sketch, "E299.bottom", {"start": v(-68.2, -99.88) * mm, "end": v(-42.8, -99.88) * mm});
            skLineSegment(sketch, "E299.top", {"start": v(-68.2, 103.66) * mm, "end": v(-42.8, 103.66) * mm});
            skLineSegment(sketch, "E299.left", {"start": v(-68.2, -99.88) * mm, "end": v(-68.2, -74.14) * mm});
            skLineSegment(sketch, "E299.right", {"start": v(135, -99.88) * mm, "end": v(135, -74.48) * mm});
            skLineSegment(sketch, "E300.MirrorCS", {"start": v(141.34, 52.52) * mm, "end": v(135, 52.52) * mm});
            skLineSegment(sketch, "E301.MirrorCS", {"start": v(141.34, -74.48) * mm, "end": v(135, -74.48) * mm});
            skLineSegment(sketch, "E302.MirrorCS", {"start": v(135, -49.08) * mm, "end": v(141.34, -49.08) * mm});
            skLineSegment(sketch, "E303.MirrorCS", {"start": v(135, 14.42) * mm, "end": v(141.34, 14.42) * mm});
            skLineSegment(sketch, "E304.MirrorCS", {"start": v(141.34, -10.98) * mm, "end": v(135, -10.98) * mm});
            skLineSegment(sketch, "E305.MirrorCS", {"start": v(135, 77.92) * mm, "end": v(141.34, 77.92) * mm});
            skLineSegment(sketch, "E306.MirrorCS", {"start": v(141.34, -49.08) * mm, "end": v(141.34, -74.48) * mm});
            skLineSegment(sketch, "E307.MirrorCS", {"start": v(141.34, 14.42) * mm, "end": v(141.34, -10.98) * mm});
            skLineSegment(sketch, "E308.MirrorCS", {"start": v(141.34, 77.92) * mm, "end": v(141.34, 52.52) * mm});
            skPoint(sketch, "E309.end.orphan", {"position": v(33.4, -99.88) * mm});
            skPoint(sketch, "E309.start.orphan", {"position": v(33.4, 103.66) * mm});
            skLineSegment(sketch, "E310.trimOffspring", {"start": v(-68.2, 14.76) * mm, "end": v(-68.2, 52.86) * mm});
            skLineSegment(sketch, "E311.trimOffspring", {"start": v(-68.2, -48.74) * mm, "end": v(-68.2, -10.64) * mm});
            skLineSegment(sketch, "E312.trimOffspring", {"start": v(-68.2, 78.26) * mm, "end": v(-68.2, 103.66) * mm});
            skLineSegment(sketch, "E313.trimOffspring", {"start": v(135, 77.92) * mm, "end": v(135, 103.66) * mm});
            skLineSegment(sketch, "E314.trimOffspring", {"start": v(135, 14.42) * mm, "end": v(135, 52.52) * mm});
            skLineSegment(sketch, "E315.trimOffspring", {"start": v(135, -49.08) * mm, "end": v(135, -10.98) * mm});
            skLineSegment(sketch, "E316.trimOffspring", {"start": v(109.6, -99.88) * mm, "end": v(135, -99.88) * mm});
            skLineSegment(sketch, "E317.trimOffspring", {"start": v(46.1, -99.88) * mm, "end": v(84.2, -99.88) * mm});
            skLineSegment(sketch, "E318.trimOffspring", {"start": v(-17.4, -99.88) * mm, "end": v(20.7, -99.88) * mm});
            skLineSegment(sketch, "E319.MirrorCS", {"start": v(109.6, 110.01) * mm, "end": v(109.6, 103.66) * mm});
            skLineSegment(sketch, "E320.MirrorCS", {"start": v(84.2, 103.66) * mm, "end": v(84.2, 110.01) * mm});
            skLineSegment(sketch, "E321.MirrorCS", {"start": v(46.1, 110.01) * mm, "end": v(46.1, 103.66) * mm});
            skLineSegment(sketch, "E322.MirrorCS", {"start": v(20.7, 103.66) * mm, "end": v(20.7, 110.01) * mm});
            skLineSegment(sketch, "E323.MirrorCS", {"start": v(-42.8, 103.66) * mm, "end": v(-42.8, 110.01) * mm});
            skLineSegment(sketch, "E324.MirrorCS", {"start": v(-17.4, 110.01) * mm, "end": v(-17.4, 103.66) * mm});
            skLineSegment(sketch, "E325.MirrorCS", {"start": v(20.7, 110.01) * mm, "end": v(46.1, 110.01) * mm});
            skLineSegment(sketch, "E326.MirrorCS", {"start": v(84.2, 110.01) * mm, "end": v(109.6, 110.01) * mm});
            skLineSegment(sketch, "E327.MirrorCS", {"start": v(-42.8, 110.01) * mm, "end": v(-17.4, 110.01) * mm});
            skLineSegment(sketch, "E328.trimOffspring", {"start": v(-17.4, 103.66) * mm, "end": v(20.7, 103.66) * mm});
            skLineSegment(sketch, "E329.trimOffspring", {"start": v(46.1, 103.66) * mm, "end": v(84.2, 103.66) * mm});
            skLineSegment(sketch, "E330.trimOffspring", {"start": v(109.6, 103.66) * mm, "end": v(135, 103.66) * mm});
            skPoint(sketch, "E331.end.orphan", {"position": v(141.34, 1.72) * mm});
            skPoint(sketch, "E331.start.orphan", {"position": v(-74.56, 2.06) * mm});
            skSolve(sketch);
        }
        {
            var Q0;
            Q0 = qSketchRegion(id + "F10", true);
            extrude(context, id + "F11", {"entities" : qUnion([Q0]), "depth" : 6.35 * mm, "offsetDistance" : 25.4 * mm});
        }
        {
            var Q0;
            Q0=makeQuery(id+"F5.opExtrude","SWEPT_FACE",FACE,{"disambiguationData":[OSD([sQuery(id+"F4.wireOp",EDGE,"E276"),sQuery(id+"F4.wireOp",EDGE,"E277")])]});
            var sketch = newSketch(context, id + "F12", { "sketchPlane" : qUnion([Q0])});
            skPoint(sketch, "E332.0", {"position": v(-74.56, -106.23) * mm});
            skPoint(sketch, "E333.0", {"position": v(135, -106.23) * mm});
            skPoint(sketch, "E334.0", {"position": v(141.34, 109.67) * mm});
            skLineSegment(sketch, "E335.bottom", {"start": v(-74.56, -106.23) * mm, "end": v(141.34, -106.23) * mm});
            skLineSegment(sketch, "E335.top", {"start": v(-74.56, 109.67) * mm, "end": v(141.34, 109.67) * mm});
            skLineSegment(sketch, "E335.left", {"start": v(-74.56, -106.23) * mm, "end": v(-74.56, 109.67) * mm});
            skLineSegment(sketch, "E335.right", {"start": v(141.34, -106.23) * mm, "end": v(141.34, 109.67) * mm});
            skSolve(sketch);
        }
        {
            var Q0;
            Q0 = qSketchRegion(id + "F12", true);
            extrude(context, id + "F13", {"entities" : qUnion([Q0]), "depth" : 6.35 * mm, "offsetDistance" : 25.4 * mm});
        }
    });
